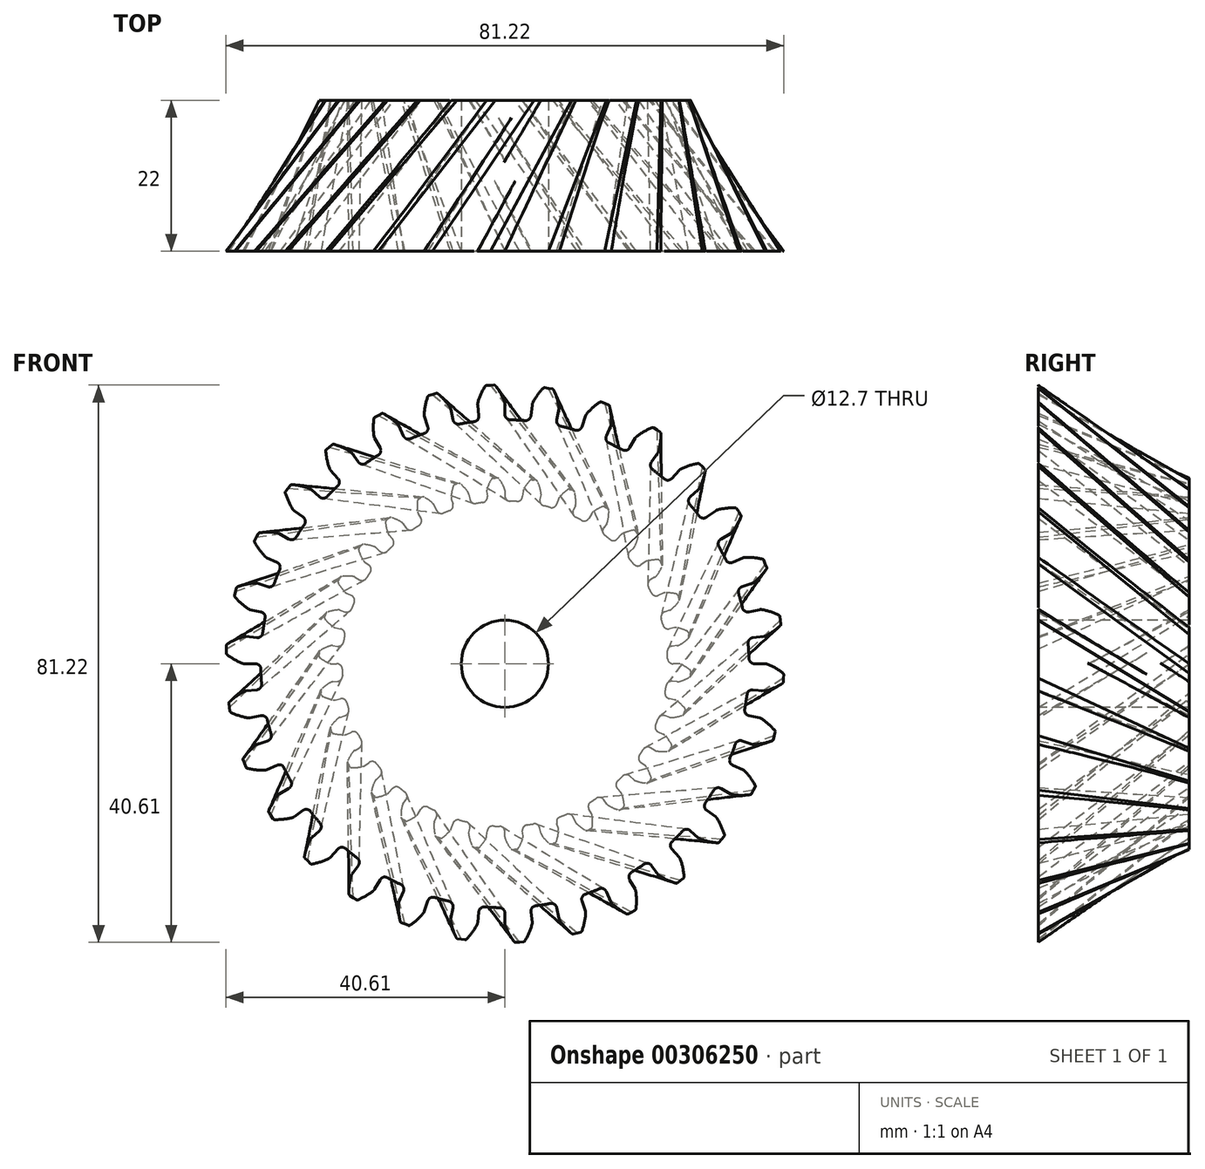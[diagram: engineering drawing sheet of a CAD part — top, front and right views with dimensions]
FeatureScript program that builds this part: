
annotation { "Feature Type Name" : "Feature", "Feature Type Description" : "" }
export const myFeature = defineFeature(function(context is Context, id is Id, definition is map)
    precondition{}
    {
        {
            var Q0;
            Q0=qCreatedBy(makeId("Front.planeOp"),FACE);
            var sketch = newSketch(context, id + "F0", { "sketchPlane" : qUnion([Q0])});
            skArc(sketch, "E0", {"start": v(-3.24, 23.49) * mm, "mid": v(-4.09, 23.36) * mm, "end": v(-4.93, 23.2) * mm});
            skArc(sketch, "E1.trimOffspring", {"start": v(-0.06, 25.55) * mm, "mid": v(-0.42, 26.29) * mm, "end": v(-0.88, 26.97) * mm});
            skLineSegment(sketch, "E2", {"start": v(-1.08, 27.07) * mm, "end": v(-1.42, 27.07) * mm});
            skLineSegment(sketch, "E3", {"start": v(0, 25.25) * mm, "end": v(0, 24.5) * mm});
            skLineSegment(sketch, "E4.MirrorCS", {"start": v(-1.76, 27.04) * mm, "end": v(-1.42, 27.07) * mm});
            skArc(sketch, "E5.MirrorCS", {"start": v(-2.61, 25.42) * mm, "mid": v(-2.33, 26.19) * mm, "end": v(-1.95, 26.92) * mm});
            skLineSegment(sketch, "E6.MirrorCS", {"start": v(-2.64, 25.1) * mm, "end": v(-2.56, 24.36) * mm});
            skArc(sketch, "E7.filletArc", {"start": v(-3.24, 23.49) * mm, "mid": v(-2.72, 23.79) * mm, "end": v(-2.56, 24.36) * mm});
            skPoint(sketch, "E8.visualSharp", {"position": v(0, 23.71) * mm});
            skPoint(sketch, "E9.visualSharp", {"position": v(-2.66, 25.26) * mm});
            skArc(sketch, "E9.filletArc", {"start": v(-2.65, 25.26) * mm, "mid": v(-2.65, 25.26) * mm, "end": v(-2.65, 25.26) * mm});
            skArc(sketch, "E10.filletArc", {"start": v(0, 24.5) * mm, "mid": v(0.22, 23.94) * mm, "end": v(0.77, 23.7) * mm});
            skArc(sketch, "E11.filletArc", {"start": v(-2.61, 25.42) * mm, "mid": v(-2.64, 25.26) * mm, "end": v(-2.64, 25.1) * mm});
            skPoint(sketch, "E12.visualSharp", {"position": v(0, 25.4) * mm});
            skArc(sketch, "E12.filletArc", {"start": v(0, 25.25) * mm, "mid": v(-0.02, 25.4) * mm, "end": v(-0.06, 25.55) * mm});
            skPoint(sketch, "E13.visualSharp", {"position": v(-1.88, 27.02) * mm});
            skArc(sketch, "E13.filletArc", {"start": v(-1.76, 27.04) * mm, "mid": v(-1.86, 27) * mm, "end": v(-1.95, 26.92) * mm});
            skPoint(sketch, "E14.visualSharp", {"position": v(-0.96, 27.07) * mm});
            skArc(sketch, "E14.filletArc", {"start": v(-0.88, 26.97) * mm, "mid": v(-0.97, 27.05) * mm, "end": v(-1.08, 27.07) * mm});
            skArc(sketch, "E15.1.0", {"start": v(-5.37, 24.98) * mm, "mid": v(-5.88, 25.63) * mm, "end": v(-6.47, 26.2) * mm});
            skPoint(sketch, "E15.1.1", {"position": v(-5.28, 24.84) * mm});
            skPoint(sketch, "E15.1.2", {"position": v(-7.85, 24.16) * mm});
            skLineSegment(sketch, "E15.1.3", {"start": v(-5.25, 24.7) * mm, "end": v(-5.1, 23.96) * mm});
            skArc(sketch, "E15.1.4", {"start": v(-7.84, 24.32) * mm, "mid": v(-7.72, 25.13) * mm, "end": v(-7.5, 25.92) * mm});
            skArc(sketch, "E15.1.5", {"start": v(-8.05, 22.3) * mm, "mid": v(-7.61, 22.7) * mm, "end": v(-7.57, 23.3) * mm});
            skPoint(sketch, "E15.1.6", {"position": v(-4.93, 23.2) * mm});
            skArc(sketch, "E15.1.7", {"start": v(-5.1, 23.96) * mm, "mid": v(-4.76, 23.46) * mm, "end": v(-4.18, 23.34) * mm});
            skPoint(sketch, "E15.1.8", {"position": v(-6.56, 26.28) * mm});
            skPoint(sketch, "E15.1.9", {"position": v(-7.46, 26.04) * mm});
            skLineSegment(sketch, "E15.1.10", {"start": v(-7.8, 24.01) * mm, "end": v(-7.57, 23.3) * mm});
            skArc(sketch, "E15.1.11", {"start": v(-5.25, 24.7) * mm, "mid": v(-5.3, 24.84) * mm, "end": v(-5.37, 24.98) * mm});
            skLineSegment(sketch, "E15.1.12", {"start": v(-7.34, 26.08) * mm, "end": v(-7.02, 26.19) * mm});
            skLineSegment(sketch, "E15.1.13", {"start": v(-6.69, 26.26) * mm, "end": v(-7.02, 26.19) * mm});
            skArc(sketch, "E15.1.14", {"start": v(-7.34, 26.08) * mm, "mid": v(-7.44, 26.02) * mm, "end": v(-7.5, 25.92) * mm});
            skArc(sketch, "E15.1.15", {"start": v(-6.47, 26.2) * mm, "mid": v(-6.57, 26.25) * mm, "end": v(-6.69, 26.26) * mm});
            skArc(sketch, "E15.1.16", {"start": v(-7.84, 24.32) * mm, "mid": v(-7.84, 24.16) * mm, "end": v(-7.8, 24.01) * mm});
            skArc(sketch, "E15.1.17", {"start": v(-7.85, 24.16) * mm, "mid": v(-7.85, 24.16) * mm, "end": v(-7.85, 24.15) * mm});
            skArc(sketch, "E15.1.18", {"start": v(-7.85, 24.16) * mm, "mid": v(-7.85, 24.16) * mm, "end": v(-7.85, 24.15) * mm});
            skArc(sketch, "E15.2.0", {"start": v(-10.45, 23.32) * mm, "mid": v(-11.08, 23.84) * mm, "end": v(-11.77, 24.28) * mm});
            skPoint(sketch, "E15.2.1", {"position": v(-10.33, 23.2) * mm});
            skPoint(sketch, "E15.2.2", {"position": v(-12.7, 22) * mm});
            skLineSegment(sketch, "E15.2.3", {"start": v(-10.27, 23.06) * mm, "end": v(-9.96, 22.37) * mm});
            skArc(sketch, "E15.2.4", {"start": v(-12.72, 22.16) * mm, "mid": v(-12.78, 22.98) * mm, "end": v(-12.73, 23.8) * mm});
            skArc(sketch, "E15.2.5", {"start": v(-12.51, 20.14) * mm, "mid": v(-12.16, 20.62) * mm, "end": v(-12.25, 21.21) * mm});
            skPoint(sketch, "E15.2.6", {"position": v(-9.64, 21.66) * mm});
            skArc(sketch, "E15.2.7", {"start": v(-9.96, 22.37) * mm, "mid": v(-9.53, 21.96) * mm, "end": v(-8.94, 21.96) * mm});
            skPoint(sketch, "E15.2.8", {"position": v(-11.88, 24.34) * mm});
            skPoint(sketch, "E15.2.9", {"position": v(-12.7, 23.92) * mm});
            skLineSegment(sketch, "E15.2.10", {"start": v(-12.62, 21.87) * mm, "end": v(-12.25, 21.21) * mm});
            skArc(sketch, "E15.2.11", {"start": v(-10.27, 23.06) * mm, "mid": v(-10.35, 23.2) * mm, "end": v(-10.45, 23.32) * mm});
            skLineSegment(sketch, "E15.2.12", {"start": v(-12.6, 23.99) * mm, "end": v(-12.3, 24.15) * mm});
            skLineSegment(sketch, "E15.2.13", {"start": v(-12, 24.3) * mm, "end": v(-12.3, 24.15) * mm});
            skArc(sketch, "E15.2.14", {"start": v(-12.6, 23.99) * mm, "mid": v(-12.68, 23.9) * mm, "end": v(-12.73, 23.8) * mm});
            skArc(sketch, "E15.2.15", {"start": v(-11.77, 24.28) * mm, "mid": v(-11.88, 24.31) * mm, "end": v(-12, 24.3) * mm});
            skArc(sketch, "E15.2.16", {"start": v(-12.72, 22.16) * mm, "mid": v(-12.69, 22) * mm, "end": v(-12.62, 21.87) * mm});
            skArc(sketch, "E15.2.17", {"start": v(-12.7, 22) * mm, "mid": v(-12.7, 22) * mm, "end": v(-12.7, 22) * mm});
            skArc(sketch, "E15.2.18", {"start": v(-12.7, 22) * mm, "mid": v(-12.7, 22) * mm, "end": v(-12.7, 22) * mm});
            skArc(sketch, "E16.1.3.0", {"start": v(-15.07, 20.64) * mm, "mid": v(-15.8, 21.02) * mm, "end": v(-16.56, 21.3) * mm});
            skPoint(sketch, "E16.4.3.0", {"position": v(-14.93, 20.55) * mm});
            skPoint(sketch, "E16.5.3.0", {"position": v(-17, 18.88) * mm});
            skLineSegment(sketch, "E16.6.3.0", {"start": v(-14.84, 20.43) * mm, "end": v(-14.4, 19.81) * mm});
            skArc(sketch, "E16.9.3.0", {"start": v(-17.05, 19.03) * mm, "mid": v(-17.28, 19.82) * mm, "end": v(-17.4, 20.63) * mm});
            skArc(sketch, "E16.13.3.0", {"start": v(-16.43, 17.1) * mm, "mid": v(-16.18, 17.64) * mm, "end": v(-16.39, 18.2) * mm});
            skPoint(sketch, "E16.17.3.0", {"position": v(-13.94, 19.18) * mm});
            skArc(sketch, "E16.18.3.0", {"start": v(-14.4, 19.81) * mm, "mid": v(-13.9, 19.5) * mm, "end": v(-13.3, 19.62) * mm});
            skPoint(sketch, "E16.22.3.0", {"position": v(-16.69, 21.34) * mm});
            skPoint(sketch, "E16.23.3.0", {"position": v(-17.4, 20.76) * mm});
            skLineSegment(sketch, "E16.24.3.0", {"start": v(-16.9, 18.76) * mm, "end": v(-16.39, 18.2) * mm});
            skArc(sketch, "E16.27.3.0", {"start": v(-14.84, 20.43) * mm, "mid": v(-14.94, 20.54) * mm, "end": v(-15.07, 20.64) * mm});
            skLineSegment(sketch, "E16.31.3.0", {"start": v(-17.31, 20.84) * mm, "end": v(-17.06, 21.07) * mm});
            skLineSegment(sketch, "E16.34.3.0", {"start": v(-16.79, 21.27) * mm, "end": v(-17.06, 21.07) * mm});
            skArc(sketch, "E16.37.3.0", {"start": v(-17.31, 20.84) * mm, "mid": v(-17.38, 20.75) * mm, "end": v(-17.4, 20.63) * mm});
            skArc(sketch, "E16.41.3.0", {"start": v(-16.56, 21.3) * mm, "mid": v(-16.68, 21.31) * mm, "end": v(-16.79, 21.27) * mm});
            skArc(sketch, "E16.45.3.0", {"start": v(-17.05, 19.03) * mm, "mid": v(-16.99, 18.89) * mm, "end": v(-16.9, 18.76) * mm});
            skArc(sketch, "E16.49.3.0", {"start": v(-17, 18.88) * mm, "mid": v(-17, 18.88) * mm, "end": v(-17, 18.87) * mm});
            skArc(sketch, "E16.53.3.0", {"start": v(-17, 18.88) * mm, "mid": v(-17, 18.88) * mm, "end": v(-17, 18.87) * mm});
            skArc(sketch, "E16.1.4.0", {"start": v(-19.03, 17.05) * mm, "mid": v(-19.82, 17.28) * mm, "end": v(-20.63, 17.4) * mm});
            skPoint(sketch, "E16.4.4.0", {"position": v(-18.88, 17) * mm});
            skPoint(sketch, "E16.5.4.0", {"position": v(-20.55, 14.93) * mm});
            skLineSegment(sketch, "E16.6.4.0", {"start": v(-18.76, 16.9) * mm, "end": v(-18.2, 16.39) * mm});
            skArc(sketch, "E16.9.4.0", {"start": v(-20.64, 15.07) * mm, "mid": v(-21.02, 15.8) * mm, "end": v(-21.3, 16.56) * mm});
            skArc(sketch, "E16.13.4.0", {"start": v(-19.62, 13.3) * mm, "mid": v(-19.5, 13.9) * mm, "end": v(-19.81, 14.4) * mm});
            skPoint(sketch, "E16.17.4.0", {"position": v(-17.62, 15.87) * mm});
            skArc(sketch, "E16.18.4.0", {"start": v(-18.2, 16.39) * mm, "mid": v(-17.64, 16.18) * mm, "end": v(-17.1, 16.43) * mm});
            skPoint(sketch, "E16.22.4.0", {"position": v(-20.76, 17.4) * mm});
            skPoint(sketch, "E16.23.4.0", {"position": v(-21.34, 16.69) * mm});
            skLineSegment(sketch, "E16.24.4.0", {"start": v(-20.43, 14.84) * mm, "end": v(-19.81, 14.4) * mm});
            skArc(sketch, "E16.27.4.0", {"start": v(-18.76, 16.9) * mm, "mid": v(-18.89, 16.99) * mm, "end": v(-19.03, 17.05) * mm});
            skLineSegment(sketch, "E16.31.4.0", {"start": v(-21.27, 16.79) * mm, "end": v(-21.07, 17.06) * mm});
            skLineSegment(sketch, "E16.34.4.0", {"start": v(-20.84, 17.31) * mm, "end": v(-21.07, 17.06) * mm});
            skArc(sketch, "E16.37.4.0", {"start": v(-21.27, 16.79) * mm, "mid": v(-21.31, 16.68) * mm, "end": v(-21.3, 16.56) * mm});
            skArc(sketch, "E16.41.4.0", {"start": v(-20.63, 17.4) * mm, "mid": v(-20.75, 17.38) * mm, "end": v(-20.84, 17.31) * mm});
            skArc(sketch, "E16.45.4.0", {"start": v(-20.64, 15.07) * mm, "mid": v(-20.54, 14.94) * mm, "end": v(-20.43, 14.84) * mm});
            skArc(sketch, "E16.49.4.0", {"start": v(-20.55, 14.93) * mm, "mid": v(-20.55, 14.93) * mm, "end": v(-20.55, 14.93) * mm});
            skArc(sketch, "E16.53.4.0", {"start": v(-20.55, 14.93) * mm, "mid": v(-20.55, 14.93) * mm, "end": v(-20.55, 14.93) * mm});
            skArc(sketch, "E16.1.5.0", {"start": v(-22.16, 12.72) * mm, "mid": v(-22.98, 12.78) * mm, "end": v(-23.8, 12.73) * mm});
            skPoint(sketch, "E16.4.5.0", {"position": v(-22, 12.7) * mm});
            skPoint(sketch, "E16.5.5.0", {"position": v(-23.2, 10.33) * mm});
            skLineSegment(sketch, "E16.6.5.0", {"start": v(-21.87, 12.62) * mm, "end": v(-21.21, 12.25) * mm});
            skArc(sketch, "E16.9.5.0", {"start": v(-23.32, 10.45) * mm, "mid": v(-23.84, 11.08) * mm, "end": v(-24.28, 11.77) * mm});
            skArc(sketch, "E16.13.5.0", {"start": v(-21.96, 8.94) * mm, "mid": v(-21.96, 9.53) * mm, "end": v(-22.37, 9.96) * mm});
            skPoint(sketch, "E16.17.5.0", {"position": v(-20.53, 11.86) * mm});
            skArc(sketch, "E16.18.5.0", {"start": v(-21.21, 12.25) * mm, "mid": v(-20.62, 12.16) * mm, "end": v(-20.14, 12.51) * mm});
            skPoint(sketch, "E16.22.5.0", {"position": v(-23.92, 12.7) * mm});
            skPoint(sketch, "E16.23.5.0", {"position": v(-24.34, 11.88) * mm});
            skLineSegment(sketch, "E16.24.5.0", {"start": v(-23.06, 10.27) * mm, "end": v(-22.37, 9.96) * mm});
            skArc(sketch, "E16.27.5.0", {"start": v(-21.87, 12.62) * mm, "mid": v(-22, 12.69) * mm, "end": v(-22.16, 12.72) * mm});
            skLineSegment(sketch, "E16.31.5.0", {"start": v(-24.3, 12) * mm, "end": v(-24.15, 12.3) * mm});
            skLineSegment(sketch, "E16.34.5.0", {"start": v(-23.99, 12.6) * mm, "end": v(-24.15, 12.3) * mm});
            skArc(sketch, "E16.37.5.0", {"start": v(-24.3, 12) * mm, "mid": v(-24.31, 11.88) * mm, "end": v(-24.28, 11.77) * mm});
            skArc(sketch, "E16.41.5.0", {"start": v(-23.8, 12.73) * mm, "mid": v(-23.9, 12.68) * mm, "end": v(-23.99, 12.6) * mm});
            skArc(sketch, "E16.45.5.0", {"start": v(-23.32, 10.45) * mm, "mid": v(-23.2, 10.35) * mm, "end": v(-23.06, 10.27) * mm});
            skArc(sketch, "E16.49.5.0", {"start": v(-23.2, 10.33) * mm, "mid": v(-23.2, 10.33) * mm, "end": v(-23.2, 10.33) * mm});
            skArc(sketch, "E16.53.5.0", {"start": v(-23.2, 10.33) * mm, "mid": v(-23.2, 10.33) * mm, "end": v(-23.2, 10.33) * mm});
            skArc(sketch, "E16.1.6.0", {"start": v(-24.32, 7.84) * mm, "mid": v(-25.13, 7.72) * mm, "end": v(-25.92, 7.5) * mm});
            skPoint(sketch, "E16.4.6.0", {"position": v(-24.16, 7.85) * mm});
            skPoint(sketch, "E16.5.6.0", {"position": v(-24.84, 5.28) * mm});
            skLineSegment(sketch, "E16.6.6.0", {"start": v(-24.01, 7.8) * mm, "end": v(-23.3, 7.57) * mm});
            skArc(sketch, "E16.9.6.0", {"start": v(-24.98, 5.37) * mm, "mid": v(-25.63, 5.88) * mm, "end": v(-26.2, 6.47) * mm});
            skArc(sketch, "E16.13.6.0", {"start": v(-23.34, 4.18) * mm, "mid": v(-23.46, 4.76) * mm, "end": v(-23.96, 5.1) * mm});
            skPoint(sketch, "E16.17.6.0", {"position": v(-22.55, 7.33) * mm});
            skArc(sketch, "E16.18.6.0", {"start": v(-23.3, 7.57) * mm, "mid": v(-22.7, 7.61) * mm, "end": v(-22.3, 8.05) * mm});
            skPoint(sketch, "E16.22.6.0", {"position": v(-26.04, 7.46) * mm});
            skPoint(sketch, "E16.23.6.0", {"position": v(-26.28, 6.56) * mm});
            skLineSegment(sketch, "E16.24.6.0", {"start": v(-24.7, 5.25) * mm, "end": v(-23.96, 5.1) * mm});
            skArc(sketch, "E16.27.6.0", {"start": v(-24.01, 7.8) * mm, "mid": v(-24.16, 7.84) * mm, "end": v(-24.32, 7.84) * mm});
            skLineSegment(sketch, "E16.31.6.0", {"start": v(-26.26, 6.69) * mm, "end": v(-26.19, 7.02) * mm});
            skLineSegment(sketch, "E16.34.6.0", {"start": v(-26.08, 7.34) * mm, "end": v(-26.19, 7.02) * mm});
            skArc(sketch, "E16.37.6.0", {"start": v(-26.26, 6.69) * mm, "mid": v(-26.25, 6.57) * mm, "end": v(-26.2, 6.47) * mm});
            skArc(sketch, "E16.41.6.0", {"start": v(-25.92, 7.5) * mm, "mid": v(-26.02, 7.44) * mm, "end": v(-26.08, 7.34) * mm});
            skArc(sketch, "E16.45.6.0", {"start": v(-24.98, 5.37) * mm, "mid": v(-24.84, 5.3) * mm, "end": v(-24.7, 5.25) * mm});
            skArc(sketch, "E16.49.6.0", {"start": v(-24.85, 5.28) * mm, "mid": v(-24.84, 5.28) * mm, "end": v(-24.84, 5.28) * mm});
            skArc(sketch, "E16.53.6.0", {"start": v(-24.85, 5.28) * mm, "mid": v(-24.84, 5.28) * mm, "end": v(-24.84, 5.28) * mm});
            skArc(sketch, "E16.1.7.0", {"start": v(-25.42, 2.61) * mm, "mid": v(-26.19, 2.33) * mm, "end": v(-26.92, 1.95) * mm});
            skPoint(sketch, "E16.4.7.0", {"position": v(-25.26, 2.66) * mm});
            skPoint(sketch, "E16.5.7.0", {"position": v(-25.4, 0) * mm});
            skLineSegment(sketch, "E16.6.7.0", {"start": v(-25.1, 2.64) * mm, "end": v(-24.36, 2.56) * mm});
            skArc(sketch, "E16.9.7.0", {"start": v(-25.55, 0.06) * mm, "mid": v(-26.29, 0.42) * mm, "end": v(-26.97, 0.88) * mm});
            skArc(sketch, "E16.13.7.0", {"start": v(-23.7, -0.77) * mm, "mid": v(-23.94, -0.22) * mm, "end": v(-24.5, 0) * mm});
            skPoint(sketch, "E16.17.7.0", {"position": v(-23.58, 2.48) * mm});
            skArc(sketch, "E16.18.7.0", {"start": v(-24.36, 2.56) * mm, "mid": v(-23.79, 2.72) * mm, "end": v(-23.49, 3.24) * mm});
            skPoint(sketch, "E16.22.7.0", {"position": v(-27.02, 1.88) * mm});
            skPoint(sketch, "E16.23.7.0", {"position": v(-27.07, 0.96) * mm});
            skLineSegment(sketch, "E16.24.7.0", {"start": v(-25.25, 0) * mm, "end": v(-24.5, 0) * mm});
            skArc(sketch, "E16.27.7.0", {"start": v(-25.1, 2.64) * mm, "mid": v(-25.26, 2.64) * mm, "end": v(-25.42, 2.61) * mm});
            skLineSegment(sketch, "E16.31.7.0", {"start": v(-27.07, 1.08) * mm, "end": v(-27.07, 1.42) * mm});
            skLineSegment(sketch, "E16.34.7.0", {"start": v(-27.04, 1.76) * mm, "end": v(-27.07, 1.42) * mm});
            skArc(sketch, "E16.37.7.0", {"start": v(-27.07, 1.08) * mm, "mid": v(-27.05, 0.97) * mm, "end": v(-26.97, 0.88) * mm});
            skArc(sketch, "E16.41.7.0", {"start": v(-26.92, 1.95) * mm, "mid": v(-27, 1.86) * mm, "end": v(-27.04, 1.76) * mm});
            skArc(sketch, "E16.45.7.0", {"start": v(-25.55, 0.06) * mm, "mid": v(-25.4, 0.02) * mm, "end": v(-25.25, 0) * mm});
            skArc(sketch, "E16.49.7.0", {"start": v(-25.4, 0) * mm, "mid": v(-25.4, 0) * mm, "end": v(-25.4, 0) * mm});
            skArc(sketch, "E16.53.7.0", {"start": v(-25.4, 0) * mm, "mid": v(-25.4, 0) * mm, "end": v(-25.4, 0) * mm});
            skArc(sketch, "E16.1.8.0", {"start": v(-25.4, -2.73) * mm, "mid": v(-26.1, -3.17) * mm, "end": v(-26.73, -3.7) * mm});
            skPoint(sketch, "E16.4.8.0", {"position": v(-25.26, -2.66) * mm});
            skPoint(sketch, "E16.5.8.0", {"position": v(-24.84, -5.28) * mm});
            skLineSegment(sketch, "E16.6.8.0", {"start": v(-25.1, -2.64) * mm, "end": v(-24.36, -2.56) * mm});
            skArc(sketch, "E16.9.8.0", {"start": v(-25, -5.25) * mm, "mid": v(-25.8, -5.05) * mm, "end": v(-26.57, -4.75) * mm});
            skArc(sketch, "E16.13.8.0", {"start": v(-23.02, -5.68) * mm, "mid": v(-23.37, -5.2) * mm, "end": v(-23.96, -5.1) * mm});
            skPoint(sketch, "E16.17.8.0", {"position": v(-23.58, -2.48) * mm});
            skArc(sketch, "E16.18.8.0", {"start": v(-24.36, -2.56) * mm, "mid": v(-23.83, -2.28) * mm, "end": v(-23.65, -1.71) * mm});
            skPoint(sketch, "E16.22.8.0", {"position": v(-26.82, -3.78) * mm});
            skPoint(sketch, "E16.23.8.0", {"position": v(-26.68, -4.7) * mm});
            skLineSegment(sketch, "E16.24.8.0", {"start": v(-24.7, -5.25) * mm, "end": v(-23.96, -5.1) * mm});
            skArc(sketch, "E16.27.8.0", {"start": v(-25.1, -2.64) * mm, "mid": v(-25.26, -2.67) * mm, "end": v(-25.4, -2.73) * mm});
            skLineSegment(sketch, "E16.31.8.0", {"start": v(-26.7, -4.57) * mm, "end": v(-26.78, -4.24) * mm});
            skLineSegment(sketch, "E16.34.8.0", {"start": v(-26.81, -3.9) * mm, "end": v(-26.78, -4.24) * mm});
            skArc(sketch, "E16.37.8.0", {"start": v(-26.7, -4.57) * mm, "mid": v(-26.66, -4.68) * mm, "end": v(-26.57, -4.75) * mm});
            skArc(sketch, "E16.41.8.0", {"start": v(-26.73, -3.7) * mm, "mid": v(-26.8, -3.79) * mm, "end": v(-26.81, -3.9) * mm});
            skArc(sketch, "E16.45.8.0", {"start": v(-25, -5.25) * mm, "mid": v(-24.85, -5.27) * mm, "end": v(-24.7, -5.25) * mm});
            skArc(sketch, "E16.49.8.0", {"start": v(-24.85, -5.28) * mm, "mid": v(-24.84, -5.28) * mm, "end": v(-24.84, -5.28) * mm});
            skArc(sketch, "E16.53.8.0", {"start": v(-24.85, -5.28) * mm, "mid": v(-24.84, -5.28) * mm, "end": v(-24.84, -5.28) * mm});
            skArc(sketch, "E16.1.9.0", {"start": v(-24.28, -7.95) * mm, "mid": v(-24.87, -8.53) * mm, "end": v(-25.38, -9.17) * mm});
            skPoint(sketch, "E16.4.9.0", {"position": v(-24.16, -7.85) * mm});
            skPoint(sketch, "E16.5.9.0", {"position": v(-23.2, -10.33) * mm});
            skLineSegment(sketch, "E16.6.9.0", {"start": v(-24.01, -7.8) * mm, "end": v(-23.3, -7.57) * mm});
            skArc(sketch, "E16.9.9.0", {"start": v(-23.37, -10.34) * mm, "mid": v(-24.19, -10.3) * mm, "end": v(-25, -10.17) * mm});
            skArc(sketch, "E16.13.9.0", {"start": v(-21.34, -10.34) * mm, "mid": v(-21.78, -9.94) * mm, "end": v(-22.37, -9.96) * mm});
            skPoint(sketch, "E16.17.9.0", {"position": v(-22.55, -7.33) * mm});
            skArc(sketch, "E16.18.9.0", {"start": v(-23.3, -7.57) * mm, "mid": v(-22.84, -7.19) * mm, "end": v(-22.78, -6.6) * mm});
            skPoint(sketch, "E16.22.9.0", {"position": v(-25.45, -9.28) * mm});
            skPoint(sketch, "E16.23.9.0", {"position": v(-25.12, -10.14) * mm});
            skLineSegment(sketch, "E16.24.9.0", {"start": v(-23.06, -10.27) * mm, "end": v(-22.37, -9.96) * mm});
            skArc(sketch, "E16.27.9.0", {"start": v(-24.01, -7.8) * mm, "mid": v(-24.15, -7.86) * mm, "end": v(-24.28, -7.95) * mm});
            skLineSegment(sketch, "E16.31.9.0", {"start": v(-25.17, -10.02) * mm, "end": v(-25.3, -9.72) * mm});
            skLineSegment(sketch, "E16.34.9.0", {"start": v(-25.41, -9.4) * mm, "end": v(-25.3, -9.72) * mm});
            skArc(sketch, "E16.37.9.0", {"start": v(-25.17, -10.02) * mm, "mid": v(-25.1, -10.12) * mm, "end": v(-25, -10.17) * mm});
            skArc(sketch, "E16.41.9.0", {"start": v(-25.38, -9.17) * mm, "mid": v(-25.42, -9.28) * mm, "end": v(-25.41, -9.4) * mm});
            skArc(sketch, "E16.45.9.0", {"start": v(-23.37, -10.34) * mm, "mid": v(-23.21, -10.32) * mm, "end": v(-23.06, -10.27) * mm});
            skArc(sketch, "E16.49.9.0", {"start": v(-23.2, -10.33) * mm, "mid": v(-23.2, -10.33) * mm, "end": v(-23.2, -10.33) * mm});
            skArc(sketch, "E16.53.9.0", {"start": v(-23.2, -10.33) * mm, "mid": v(-23.2, -10.33) * mm, "end": v(-23.2, -10.33) * mm});
            skArc(sketch, "E16.1.10.0", {"start": v(-22.1, -12.83) * mm, "mid": v(-22.55, -13.51) * mm, "end": v(-22.92, -14.25) * mm});
            skPoint(sketch, "E16.4.10.0", {"position": v(-22, -12.7) * mm});
            skPoint(sketch, "E16.5.10.0", {"position": v(-20.55, -14.93) * mm});
            skLineSegment(sketch, "E16.6.10.0", {"start": v(-21.87, -12.62) * mm, "end": v(-21.21, -12.25) * mm});
            skArc(sketch, "E16.9.10.0", {"start": v(-20.7, -14.97) * mm, "mid": v(-21.52, -15.1) * mm, "end": v(-22.34, -15.14) * mm});
            skArc(sketch, "E16.13.10.0", {"start": v(-18.72, -14.55) * mm, "mid": v(-19.24, -14.25) * mm, "end": v(-19.81, -14.4) * mm});
            skPoint(sketch, "E16.17.10.0", {"position": v(-20.53, -11.86) * mm});
            skArc(sketch, "E16.18.10.0", {"start": v(-21.21, -12.25) * mm, "mid": v(-20.84, -11.78) * mm, "end": v(-20.9, -11.18) * mm});
            skPoint(sketch, "E16.22.10.0", {"position": v(-22.97, -14.36) * mm});
            skPoint(sketch, "E16.23.10.0", {"position": v(-22.46, -15.14) * mm});
            skLineSegment(sketch, "E16.24.10.0", {"start": v(-20.43, -14.84) * mm, "end": v(-19.81, -14.4) * mm});
            skArc(sketch, "E16.27.10.0", {"start": v(-21.87, -12.62) * mm, "mid": v(-22, -12.71) * mm, "end": v(-22.1, -12.83) * mm});
            skLineSegment(sketch, "E16.31.10.0", {"start": v(-22.54, -15.04) * mm, "end": v(-22.74, -14.76) * mm});
            skLineSegment(sketch, "E16.34.10.0", {"start": v(-22.9, -14.47) * mm, "end": v(-22.74, -14.76) * mm});
            skArc(sketch, "E16.37.10.0", {"start": v(-22.54, -15.04) * mm, "mid": v(-22.45, -15.11) * mm, "end": v(-22.34, -15.14) * mm});
            skArc(sketch, "E16.41.10.0", {"start": v(-22.92, -14.25) * mm, "mid": v(-22.94, -14.36) * mm, "end": v(-22.9, -14.47) * mm});
            skArc(sketch, "E16.45.10.0", {"start": v(-20.7, -14.97) * mm, "mid": v(-20.56, -14.92) * mm, "end": v(-20.43, -14.84) * mm});
            skArc(sketch, "E16.49.10.0", {"start": v(-20.55, -14.93) * mm, "mid": v(-20.55, -14.93) * mm, "end": v(-20.55, -14.93) * mm});
            skArc(sketch, "E16.53.10.0", {"start": v(-20.55, -14.93) * mm, "mid": v(-20.55, -14.93) * mm, "end": v(-20.55, -14.93) * mm});
            skArc(sketch, "E16.1.11.0", {"start": v(-18.95, -17.14) * mm, "mid": v(-19.25, -17.9) * mm, "end": v(-19.46, -18.7) * mm});
            skPoint(sketch, "E16.4.11.0", {"position": v(-18.88, -17) * mm});
            skPoint(sketch, "E16.5.11.0", {"position": v(-17, -18.88) * mm});
            skLineSegment(sketch, "E16.6.11.0", {"start": v(-18.76, -16.9) * mm, "end": v(-18.2, -16.39) * mm});
            skArc(sketch, "E16.9.11.0", {"start": v(-17.14, -18.95) * mm, "mid": v(-17.9, -19.25) * mm, "end": v(-18.7, -19.46) * mm});
            skArc(sketch, "E16.13.11.0", {"start": v(-15.29, -18.13) * mm, "mid": v(-15.85, -17.94) * mm, "end": v(-16.39, -18.2) * mm});
            skPoint(sketch, "E16.17.11.0", {"position": v(-17.62, -15.87) * mm});
            skArc(sketch, "E16.18.11.0", {"start": v(-18.2, -16.39) * mm, "mid": v(-17.94, -15.85) * mm, "end": v(-18.13, -15.29) * mm});
            skPoint(sketch, "E16.22.11.0", {"position": v(-19.48, -18.83) * mm});
            skPoint(sketch, "E16.23.11.0", {"position": v(-18.83, -19.48) * mm});
            skLineSegment(sketch, "E16.24.11.0", {"start": v(-16.9, -18.76) * mm, "end": v(-16.39, -18.2) * mm});
            skArc(sketch, "E16.27.11.0", {"start": v(-18.76, -16.9) * mm, "mid": v(-18.87, -17) * mm, "end": v(-18.95, -17.14) * mm});
            skLineSegment(sketch, "E16.31.11.0", {"start": v(-18.92, -19.4) * mm, "end": v(-19.17, -19.17) * mm});
            skLineSegment(sketch, "E16.34.11.0", {"start": v(-19.4, -18.92) * mm, "end": v(-19.17, -19.17) * mm});
            skArc(sketch, "E16.37.11.0", {"start": v(-18.92, -19.4) * mm, "mid": v(-18.82, -19.45) * mm, "end": v(-18.7, -19.46) * mm});
            skArc(sketch, "E16.41.11.0", {"start": v(-19.46, -18.7) * mm, "mid": v(-19.45, -18.82) * mm, "end": v(-19.4, -18.92) * mm});
            skArc(sketch, "E16.45.11.0", {"start": v(-17.14, -18.95) * mm, "mid": v(-17, -18.87) * mm, "end": v(-16.9, -18.76) * mm});
            skArc(sketch, "E16.49.11.0", {"start": v(-17, -18.88) * mm, "mid": v(-17, -18.88) * mm, "end": v(-17, -18.87) * mm});
            skArc(sketch, "E16.53.11.0", {"start": v(-17, -18.88) * mm, "mid": v(-17, -18.88) * mm, "end": v(-17, -18.87) * mm});
            skArc(sketch, "E16.1.12.0", {"start": v(-14.97, -20.7) * mm, "mid": v(-15.1, -21.52) * mm, "end": v(-15.14, -22.34) * mm});
            skPoint(sketch, "E16.4.12.0", {"position": v(-14.93, -20.55) * mm});
            skPoint(sketch, "E16.5.12.0", {"position": v(-12.7, -22) * mm});
            skLineSegment(sketch, "E16.6.12.0", {"start": v(-14.84, -20.43) * mm, "end": v(-14.4, -19.81) * mm});
            skArc(sketch, "E16.9.12.0", {"start": v(-12.83, -22.1) * mm, "mid": v(-13.51, -22.55) * mm, "end": v(-14.25, -22.92) * mm});
            skArc(sketch, "E16.13.12.0", {"start": v(-11.18, -20.9) * mm, "mid": v(-11.78, -20.84) * mm, "end": v(-12.25, -21.21) * mm});
            skPoint(sketch, "E16.17.12.0", {"position": v(-13.94, -19.18) * mm});
            skArc(sketch, "E16.18.12.0", {"start": v(-14.4, -19.81) * mm, "mid": v(-14.25, -19.24) * mm, "end": v(-14.55, -18.72) * mm});
            skPoint(sketch, "E16.22.12.0", {"position": v(-15.14, -22.46) * mm});
            skPoint(sketch, "E16.23.12.0", {"position": v(-14.36, -22.97) * mm});
            skLineSegment(sketch, "E16.24.12.0", {"start": v(-12.62, -21.87) * mm, "end": v(-12.25, -21.21) * mm});
            skArc(sketch, "E16.27.12.0", {"start": v(-14.84, -20.43) * mm, "mid": v(-14.92, -20.56) * mm, "end": v(-14.97, -20.7) * mm});
            skLineSegment(sketch, "E16.31.12.0", {"start": v(-14.47, -22.9) * mm, "end": v(-14.76, -22.74) * mm});
            skLineSegment(sketch, "E16.34.12.0", {"start": v(-15.04, -22.54) * mm, "end": v(-14.76, -22.74) * mm});
            skArc(sketch, "E16.37.12.0", {"start": v(-14.47, -22.9) * mm, "mid": v(-14.36, -22.94) * mm, "end": v(-14.25, -22.92) * mm});
            skArc(sketch, "E16.41.12.0", {"start": v(-15.14, -22.34) * mm, "mid": v(-15.11, -22.45) * mm, "end": v(-15.04, -22.54) * mm});
            skArc(sketch, "E16.45.12.0", {"start": v(-12.83, -22.1) * mm, "mid": v(-12.71, -22) * mm, "end": v(-12.62, -21.87) * mm});
            skArc(sketch, "E16.49.12.0", {"start": v(-12.7, -22) * mm, "mid": v(-12.7, -22) * mm, "end": v(-12.7, -22) * mm});
            skArc(sketch, "E16.53.12.0", {"start": v(-12.7, -22) * mm, "mid": v(-12.7, -22) * mm, "end": v(-12.7, -22) * mm});
            skArc(sketch, "E16.1.13.0", {"start": v(-10.34, -23.37) * mm, "mid": v(-10.3, -24.19) * mm, "end": v(-10.17, -25) * mm});
            skPoint(sketch, "E16.4.13.0", {"position": v(-10.33, -23.2) * mm});
            skPoint(sketch, "E16.5.13.0", {"position": v(-7.85, -24.16) * mm});
            skLineSegment(sketch, "E16.6.13.0", {"start": v(-10.27, -23.06) * mm, "end": v(-9.96, -22.37) * mm});
            skArc(sketch, "E16.9.13.0", {"start": v(-7.95, -24.28) * mm, "mid": v(-8.53, -24.87) * mm, "end": v(-9.17, -25.38) * mm});
            skArc(sketch, "E16.13.13.0", {"start": v(-6.6, -22.78) * mm, "mid": v(-7.19, -22.84) * mm, "end": v(-7.57, -23.3) * mm});
            skPoint(sketch, "E16.17.13.0", {"position": v(-9.64, -21.66) * mm});
            skArc(sketch, "E16.18.13.0", {"start": v(-9.96, -22.37) * mm, "mid": v(-9.94, -21.78) * mm, "end": v(-10.34, -21.34) * mm});
            skPoint(sketch, "E16.22.13.0", {"position": v(-10.14, -25.12) * mm});
            skPoint(sketch, "E16.23.13.0", {"position": v(-9.28, -25.45) * mm});
            skLineSegment(sketch, "E16.24.13.0", {"start": v(-7.8, -24.01) * mm, "end": v(-7.57, -23.3) * mm});
            skArc(sketch, "E16.27.13.0", {"start": v(-10.27, -23.06) * mm, "mid": v(-10.32, -23.21) * mm, "end": v(-10.34, -23.37) * mm});
            skLineSegment(sketch, "E16.31.13.0", {"start": v(-9.4, -25.41) * mm, "end": v(-9.72, -25.3) * mm});
            skLineSegment(sketch, "E16.34.13.0", {"start": v(-10.02, -25.17) * mm, "end": v(-9.72, -25.3) * mm});
            skArc(sketch, "E16.37.13.0", {"start": v(-9.4, -25.41) * mm, "mid": v(-9.28, -25.42) * mm, "end": v(-9.17, -25.38) * mm});
            skArc(sketch, "E16.41.13.0", {"start": v(-10.17, -25) * mm, "mid": v(-10.12, -25.1) * mm, "end": v(-10.02, -25.17) * mm});
            skArc(sketch, "E16.45.13.0", {"start": v(-7.95, -24.28) * mm, "mid": v(-7.86, -24.15) * mm, "end": v(-7.8, -24.01) * mm});
            skArc(sketch, "E16.49.13.0", {"start": v(-7.85, -24.16) * mm, "mid": v(-7.85, -24.16) * mm, "end": v(-7.85, -24.15) * mm});
            skArc(sketch, "E16.53.13.0", {"start": v(-7.85, -24.16) * mm, "mid": v(-7.85, -24.16) * mm, "end": v(-7.85, -24.15) * mm});
            skArc(sketch, "E16.1.14.0", {"start": v(-5.25, -25) * mm, "mid": v(-5.05, -25.8) * mm, "end": v(-4.75, -26.57) * mm});
            skPoint(sketch, "E16.4.14.0", {"position": v(-5.28, -24.84) * mm});
            skPoint(sketch, "E16.5.14.0", {"position": v(-2.66, -25.26) * mm});
            skLineSegment(sketch, "E16.6.14.0", {"start": v(-5.25, -24.7) * mm, "end": v(-5.1, -23.96) * mm});
            skArc(sketch, "E16.9.14.0", {"start": v(-2.73, -25.4) * mm, "mid": v(-3.17, -26.1) * mm, "end": v(-3.7, -26.73) * mm});
            skArc(sketch, "E16.13.14.0", {"start": v(-1.71, -23.65) * mm, "mid": v(-2.28, -23.83) * mm, "end": v(-2.56, -24.36) * mm});
            skPoint(sketch, "E16.17.14.0", {"position": v(-4.93, -23.2) * mm});
            skArc(sketch, "E16.18.14.0", {"start": v(-5.1, -23.96) * mm, "mid": v(-5.2, -23.37) * mm, "end": v(-5.68, -23.02) * mm});
            skPoint(sketch, "E16.22.14.0", {"position": v(-4.7, -26.68) * mm});
            skPoint(sketch, "E16.23.14.0", {"position": v(-3.78, -26.82) * mm});
            skLineSegment(sketch, "E16.24.14.0", {"start": v(-2.64, -25.1) * mm, "end": v(-2.56, -24.36) * mm});
            skArc(sketch, "E16.27.14.0", {"start": v(-5.25, -24.7) * mm, "mid": v(-5.27, -24.85) * mm, "end": v(-5.25, -25) * mm});
            skLineSegment(sketch, "E16.31.14.0", {"start": v(-3.9, -26.81) * mm, "end": v(-4.24, -26.78) * mm});
            skLineSegment(sketch, "E16.34.14.0", {"start": v(-4.57, -26.7) * mm, "end": v(-4.24, -26.78) * mm});
            skArc(sketch, "E16.37.14.0", {"start": v(-3.9, -26.81) * mm, "mid": v(-3.79, -26.8) * mm, "end": v(-3.7, -26.73) * mm});
            skArc(sketch, "E16.41.14.0", {"start": v(-4.75, -26.57) * mm, "mid": v(-4.68, -26.66) * mm, "end": v(-4.57, -26.7) * mm});
            skArc(sketch, "E16.45.14.0", {"start": v(-2.73, -25.4) * mm, "mid": v(-2.67, -25.26) * mm, "end": v(-2.64, -25.1) * mm});
            skArc(sketch, "E16.49.14.0", {"start": v(-2.66, -25.26) * mm, "mid": v(-2.66, -25.26) * mm, "end": v(-2.65, -25.26) * mm});
            skArc(sketch, "E16.53.14.0", {"start": v(-2.66, -25.26) * mm, "mid": v(-2.66, -25.26) * mm, "end": v(-2.65, -25.26) * mm});
            skArc(sketch, "E16.1.15.0", {"start": v(0.06, -25.55) * mm, "mid": v(0.42, -26.29) * mm, "end": v(0.88, -26.97) * mm});
            skPoint(sketch, "E16.4.15.0", {"position": v(0, -25.4) * mm});
            skPoint(sketch, "E16.5.15.0", {"position": v(2.66, -25.26) * mm});
            skLineSegment(sketch, "E16.6.15.0", {"start": v(0, -25.25) * mm, "end": v(0, -24.5) * mm});
            skArc(sketch, "E16.9.15.0", {"start": v(2.61, -25.42) * mm, "mid": v(2.33, -26.19) * mm, "end": v(1.95, -26.92) * mm});
            skArc(sketch, "E16.13.15.0", {"start": v(3.24, -23.49) * mm, "mid": v(2.72, -23.79) * mm, "end": v(2.56, -24.36) * mm});
            skPoint(sketch, "E16.17.15.0", {"position": v(0, -23.71) * mm});
            skArc(sketch, "E16.18.15.0", {"start": v(0, -24.5) * mm, "mid": v(-0.22, -23.94) * mm, "end": v(-0.77, -23.7) * mm});
            skPoint(sketch, "E16.22.15.0", {"position": v(0.96, -27.07) * mm});
            skPoint(sketch, "E16.23.15.0", {"position": v(1.88, -27.02) * mm});
            skLineSegment(sketch, "E16.24.15.0", {"start": v(2.64, -25.1) * mm, "end": v(2.56, -24.36) * mm});
            skArc(sketch, "E16.27.15.0", {"start": v(0, -25.25) * mm, "mid": v(0.02, -25.4) * mm, "end": v(0.06, -25.55) * mm});
            skLineSegment(sketch, "E16.31.15.0", {"start": v(1.76, -27.04) * mm, "end": v(1.42, -27.07) * mm});
            skLineSegment(sketch, "E16.34.15.0", {"start": v(1.08, -27.07) * mm, "end": v(1.42, -27.07) * mm});
            skArc(sketch, "E16.37.15.0", {"start": v(1.76, -27.04) * mm, "mid": v(1.86, -27) * mm, "end": v(1.95, -26.92) * mm});
            skArc(sketch, "E16.41.15.0", {"start": v(0.88, -26.97) * mm, "mid": v(0.97, -27.05) * mm, "end": v(1.08, -27.07) * mm});
            skArc(sketch, "E16.45.15.0", {"start": v(2.61, -25.42) * mm, "mid": v(2.64, -25.26) * mm, "end": v(2.64, -25.1) * mm});
            skArc(sketch, "E16.49.15.0", {"start": v(2.65, -25.26) * mm, "mid": v(2.65, -25.26) * mm, "end": v(2.65, -25.26) * mm});
            skArc(sketch, "E16.53.15.0", {"start": v(2.65, -25.26) * mm, "mid": v(2.65, -25.26) * mm, "end": v(2.65, -25.26) * mm});
            skArc(sketch, "E16.1.16.0", {"start": v(5.37, -24.98) * mm, "mid": v(5.88, -25.63) * mm, "end": v(6.47, -26.2) * mm});
            skPoint(sketch, "E16.4.16.0", {"position": v(5.28, -24.84) * mm});
            skPoint(sketch, "E16.5.16.0", {"position": v(7.85, -24.16) * mm});
            skLineSegment(sketch, "E16.6.16.0", {"start": v(5.25, -24.7) * mm, "end": v(5.1, -23.96) * mm});
            skArc(sketch, "E16.9.16.0", {"start": v(7.84, -24.32) * mm, "mid": v(7.72, -25.13) * mm, "end": v(7.5, -25.92) * mm});
            skArc(sketch, "E16.13.16.0", {"start": v(8.05, -22.3) * mm, "mid": v(7.61, -22.7) * mm, "end": v(7.57, -23.3) * mm});
            skPoint(sketch, "E16.17.16.0", {"position": v(4.93, -23.2) * mm});
            skArc(sketch, "E16.18.16.0", {"start": v(5.1, -23.96) * mm, "mid": v(4.76, -23.46) * mm, "end": v(4.18, -23.34) * mm});
            skPoint(sketch, "E16.22.16.0", {"position": v(6.56, -26.28) * mm});
            skPoint(sketch, "E16.23.16.0", {"position": v(7.46, -26.04) * mm});
            skLineSegment(sketch, "E16.24.16.0", {"start": v(7.8, -24.01) * mm, "end": v(7.57, -23.3) * mm});
            skArc(sketch, "E16.27.16.0", {"start": v(5.25, -24.7) * mm, "mid": v(5.3, -24.84) * mm, "end": v(5.37, -24.98) * mm});
            skLineSegment(sketch, "E16.31.16.0", {"start": v(7.34, -26.08) * mm, "end": v(7.02, -26.19) * mm});
            skLineSegment(sketch, "E16.34.16.0", {"start": v(6.69, -26.26) * mm, "end": v(7.02, -26.19) * mm});
            skArc(sketch, "E16.37.16.0", {"start": v(7.34, -26.08) * mm, "mid": v(7.44, -26.02) * mm, "end": v(7.5, -25.92) * mm});
            skArc(sketch, "E16.41.16.0", {"start": v(6.47, -26.2) * mm, "mid": v(6.57, -26.25) * mm, "end": v(6.69, -26.26) * mm});
            skArc(sketch, "E16.45.16.0", {"start": v(7.84, -24.32) * mm, "mid": v(7.84, -24.16) * mm, "end": v(7.8, -24.01) * mm});
            skArc(sketch, "E16.49.16.0", {"start": v(7.85, -24.16) * mm, "mid": v(7.85, -24.16) * mm, "end": v(7.85, -24.15) * mm});
            skArc(sketch, "E16.53.16.0", {"start": v(7.85, -24.16) * mm, "mid": v(7.85, -24.16) * mm, "end": v(7.85, -24.15) * mm});
            skArc(sketch, "E16.1.17.0", {"start": v(10.45, -23.32) * mm, "mid": v(11.08, -23.84) * mm, "end": v(11.77, -24.28) * mm});
            skPoint(sketch, "E16.4.17.0", {"position": v(10.33, -23.2) * mm});
            skPoint(sketch, "E16.5.17.0", {"position": v(12.7, -22) * mm});
            skLineSegment(sketch, "E16.6.17.0", {"start": v(10.27, -23.06) * mm, "end": v(9.96, -22.37) * mm});
            skArc(sketch, "E16.9.17.0", {"start": v(12.72, -22.16) * mm, "mid": v(12.78, -22.98) * mm, "end": v(12.73, -23.8) * mm});
            skArc(sketch, "E16.13.17.0", {"start": v(12.51, -20.14) * mm, "mid": v(12.16, -20.62) * mm, "end": v(12.25, -21.21) * mm});
            skPoint(sketch, "E16.17.17.0", {"position": v(9.64, -21.66) * mm});
            skArc(sketch, "E16.18.17.0", {"start": v(9.96, -22.37) * mm, "mid": v(9.53, -21.96) * mm, "end": v(8.94, -21.96) * mm});
            skPoint(sketch, "E16.22.17.0", {"position": v(11.88, -24.34) * mm});
            skPoint(sketch, "E16.23.17.0", {"position": v(12.7, -23.92) * mm});
            skLineSegment(sketch, "E16.24.17.0", {"start": v(12.62, -21.87) * mm, "end": v(12.25, -21.21) * mm});
            skArc(sketch, "E16.27.17.0", {"start": v(10.27, -23.06) * mm, "mid": v(10.35, -23.2) * mm, "end": v(10.45, -23.32) * mm});
            skLineSegment(sketch, "E16.31.17.0", {"start": v(12.6, -23.99) * mm, "end": v(12.3, -24.15) * mm});
            skLineSegment(sketch, "E16.34.17.0", {"start": v(12, -24.3) * mm, "end": v(12.3, -24.15) * mm});
            skArc(sketch, "E16.37.17.0", {"start": v(12.6, -23.99) * mm, "mid": v(12.68, -23.9) * mm, "end": v(12.73, -23.8) * mm});
            skArc(sketch, "E16.41.17.0", {"start": v(11.77, -24.28) * mm, "mid": v(11.88, -24.31) * mm, "end": v(12, -24.3) * mm});
            skArc(sketch, "E16.45.17.0", {"start": v(12.72, -22.16) * mm, "mid": v(12.69, -22) * mm, "end": v(12.62, -21.87) * mm});
            skArc(sketch, "E16.49.17.0", {"start": v(12.7, -22) * mm, "mid": v(12.7, -22) * mm, "end": v(12.7, -22) * mm});
            skArc(sketch, "E16.53.17.0", {"start": v(12.7, -22) * mm, "mid": v(12.7, -22) * mm, "end": v(12.7, -22) * mm});
            skArc(sketch, "E16.1.18.0", {"start": v(15.07, -20.64) * mm, "mid": v(15.8, -21.02) * mm, "end": v(16.56, -21.3) * mm});
            skPoint(sketch, "E16.4.18.0", {"position": v(14.93, -20.55) * mm});
            skPoint(sketch, "E16.5.18.0", {"position": v(17, -18.88) * mm});
            skLineSegment(sketch, "E16.6.18.0", {"start": v(14.84, -20.43) * mm, "end": v(14.4, -19.81) * mm});
            skArc(sketch, "E16.9.18.0", {"start": v(17.05, -19.03) * mm, "mid": v(17.28, -19.82) * mm, "end": v(17.4, -20.63) * mm});
            skArc(sketch, "E16.13.18.0", {"start": v(16.43, -17.1) * mm, "mid": v(16.18, -17.64) * mm, "end": v(16.39, -18.2) * mm});
            skPoint(sketch, "E16.17.18.0", {"position": v(13.94, -19.18) * mm});
            skArc(sketch, "E16.18.18.0", {"start": v(14.4, -19.81) * mm, "mid": v(13.9, -19.5) * mm, "end": v(13.3, -19.62) * mm});
            skPoint(sketch, "E16.22.18.0", {"position": v(16.69, -21.34) * mm});
            skPoint(sketch, "E16.23.18.0", {"position": v(17.4, -20.76) * mm});
            skLineSegment(sketch, "E16.24.18.0", {"start": v(16.9, -18.76) * mm, "end": v(16.39, -18.2) * mm});
            skArc(sketch, "E16.27.18.0", {"start": v(14.84, -20.43) * mm, "mid": v(14.94, -20.54) * mm, "end": v(15.07, -20.64) * mm});
            skLineSegment(sketch, "E16.31.18.0", {"start": v(17.31, -20.84) * mm, "end": v(17.06, -21.07) * mm});
            skLineSegment(sketch, "E16.34.18.0", {"start": v(16.79, -21.27) * mm, "end": v(17.06, -21.07) * mm});
            skArc(sketch, "E16.37.18.0", {"start": v(17.31, -20.84) * mm, "mid": v(17.38, -20.75) * mm, "end": v(17.4, -20.63) * mm});
            skArc(sketch, "E16.41.18.0", {"start": v(16.56, -21.3) * mm, "mid": v(16.68, -21.31) * mm, "end": v(16.79, -21.27) * mm});
            skArc(sketch, "E16.45.18.0", {"start": v(17.05, -19.03) * mm, "mid": v(16.99, -18.89) * mm, "end": v(16.9, -18.76) * mm});
            skArc(sketch, "E16.49.18.0", {"start": v(17, -18.88) * mm, "mid": v(17, -18.88) * mm, "end": v(17, -18.87) * mm});
            skArc(sketch, "E16.53.18.0", {"start": v(17, -18.88) * mm, "mid": v(17, -18.88) * mm, "end": v(17, -18.87) * mm});
            skArc(sketch, "E16.1.19.0", {"start": v(19.03, -17.05) * mm, "mid": v(19.82, -17.28) * mm, "end": v(20.63, -17.4) * mm});
            skPoint(sketch, "E16.4.19.0", {"position": v(18.88, -17) * mm});
            skPoint(sketch, "E16.5.19.0", {"position": v(20.55, -14.93) * mm});
            skLineSegment(sketch, "E16.6.19.0", {"start": v(18.76, -16.9) * mm, "end": v(18.2, -16.39) * mm});
            skArc(sketch, "E16.9.19.0", {"start": v(20.64, -15.07) * mm, "mid": v(21.02, -15.8) * mm, "end": v(21.3, -16.56) * mm});
            skArc(sketch, "E16.13.19.0", {"start": v(19.62, -13.3) * mm, "mid": v(19.5, -13.9) * mm, "end": v(19.81, -14.4) * mm});
            skPoint(sketch, "E16.17.19.0", {"position": v(17.62, -15.87) * mm});
            skArc(sketch, "E16.18.19.0", {"start": v(18.2, -16.39) * mm, "mid": v(17.64, -16.18) * mm, "end": v(17.1, -16.43) * mm});
            skPoint(sketch, "E16.22.19.0", {"position": v(20.76, -17.4) * mm});
            skPoint(sketch, "E16.23.19.0", {"position": v(21.34, -16.69) * mm});
            skLineSegment(sketch, "E16.24.19.0", {"start": v(20.43, -14.84) * mm, "end": v(19.81, -14.4) * mm});
            skArc(sketch, "E16.27.19.0", {"start": v(18.76, -16.9) * mm, "mid": v(18.89, -16.99) * mm, "end": v(19.03, -17.05) * mm});
            skLineSegment(sketch, "E16.31.19.0", {"start": v(21.27, -16.79) * mm, "end": v(21.07, -17.06) * mm});
            skLineSegment(sketch, "E16.34.19.0", {"start": v(20.84, -17.31) * mm, "end": v(21.07, -17.06) * mm});
            skArc(sketch, "E16.37.19.0", {"start": v(21.27, -16.79) * mm, "mid": v(21.31, -16.68) * mm, "end": v(21.3, -16.56) * mm});
            skArc(sketch, "E16.41.19.0", {"start": v(20.63, -17.4) * mm, "mid": v(20.75, -17.38) * mm, "end": v(20.84, -17.31) * mm});
            skArc(sketch, "E16.45.19.0", {"start": v(20.64, -15.07) * mm, "mid": v(20.54, -14.94) * mm, "end": v(20.43, -14.84) * mm});
            skArc(sketch, "E16.49.19.0", {"start": v(20.55, -14.93) * mm, "mid": v(20.55, -14.93) * mm, "end": v(20.55, -14.93) * mm});
            skArc(sketch, "E16.53.19.0", {"start": v(20.55, -14.93) * mm, "mid": v(20.55, -14.93) * mm, "end": v(20.55, -14.93) * mm});
            skArc(sketch, "E16.1.20.0", {"start": v(22.16, -12.72) * mm, "mid": v(22.98, -12.78) * mm, "end": v(23.8, -12.73) * mm});
            skPoint(sketch, "E16.4.20.0", {"position": v(22, -12.7) * mm});
            skPoint(sketch, "E16.5.20.0", {"position": v(23.2, -10.33) * mm});
            skLineSegment(sketch, "E16.6.20.0", {"start": v(21.87, -12.62) * mm, "end": v(21.21, -12.25) * mm});
            skArc(sketch, "E16.9.20.0", {"start": v(23.32, -10.45) * mm, "mid": v(23.84, -11.08) * mm, "end": v(24.28, -11.77) * mm});
            skArc(sketch, "E16.13.20.0", {"start": v(21.96, -8.94) * mm, "mid": v(21.96, -9.53) * mm, "end": v(22.37, -9.96) * mm});
            skPoint(sketch, "E16.17.20.0", {"position": v(20.53, -11.86) * mm});
            skArc(sketch, "E16.18.20.0", {"start": v(21.21, -12.25) * mm, "mid": v(20.62, -12.16) * mm, "end": v(20.14, -12.51) * mm});
            skPoint(sketch, "E16.22.20.0", {"position": v(23.92, -12.7) * mm});
            skPoint(sketch, "E16.23.20.0", {"position": v(24.34, -11.88) * mm});
            skLineSegment(sketch, "E16.24.20.0", {"start": v(23.06, -10.27) * mm, "end": v(22.37, -9.96) * mm});
            skArc(sketch, "E16.27.20.0", {"start": v(21.87, -12.62) * mm, "mid": v(22, -12.69) * mm, "end": v(22.16, -12.72) * mm});
            skLineSegment(sketch, "E16.31.20.0", {"start": v(24.3, -12) * mm, "end": v(24.15, -12.3) * mm});
            skLineSegment(sketch, "E16.34.20.0", {"start": v(23.99, -12.6) * mm, "end": v(24.15, -12.3) * mm});
            skArc(sketch, "E16.37.20.0", {"start": v(24.3, -12) * mm, "mid": v(24.31, -11.88) * mm, "end": v(24.28, -11.77) * mm});
            skArc(sketch, "E16.41.20.0", {"start": v(23.8, -12.73) * mm, "mid": v(23.9, -12.68) * mm, "end": v(23.99, -12.6) * mm});
            skArc(sketch, "E16.45.20.0", {"start": v(23.32, -10.45) * mm, "mid": v(23.2, -10.35) * mm, "end": v(23.06, -10.27) * mm});
            skArc(sketch, "E16.49.20.0", {"start": v(23.2, -10.33) * mm, "mid": v(23.2, -10.33) * mm, "end": v(23.2, -10.33) * mm});
            skArc(sketch, "E16.53.20.0", {"start": v(23.2, -10.33) * mm, "mid": v(23.2, -10.33) * mm, "end": v(23.2, -10.33) * mm});
            skArc(sketch, "E16.1.21.0", {"start": v(24.32, -7.84) * mm, "mid": v(25.13, -7.72) * mm, "end": v(25.92, -7.5) * mm});
            skPoint(sketch, "E16.4.21.0", {"position": v(24.16, -7.85) * mm});
            skPoint(sketch, "E16.5.21.0", {"position": v(24.84, -5.28) * mm});
            skLineSegment(sketch, "E16.6.21.0", {"start": v(24.01, -7.8) * mm, "end": v(23.3, -7.57) * mm});
            skArc(sketch, "E16.9.21.0", {"start": v(24.98, -5.37) * mm, "mid": v(25.63, -5.88) * mm, "end": v(26.2, -6.47) * mm});
            skArc(sketch, "E16.13.21.0", {"start": v(23.34, -4.18) * mm, "mid": v(23.46, -4.76) * mm, "end": v(23.96, -5.1) * mm});
            skPoint(sketch, "E16.17.21.0", {"position": v(22.55, -7.33) * mm});
            skArc(sketch, "E16.18.21.0", {"start": v(23.3, -7.57) * mm, "mid": v(22.7, -7.61) * mm, "end": v(22.3, -8.05) * mm});
            skPoint(sketch, "E16.22.21.0", {"position": v(26.04, -7.46) * mm});
            skPoint(sketch, "E16.23.21.0", {"position": v(26.28, -6.56) * mm});
            skLineSegment(sketch, "E16.24.21.0", {"start": v(24.7, -5.25) * mm, "end": v(23.96, -5.1) * mm});
            skArc(sketch, "E16.27.21.0", {"start": v(24.01, -7.8) * mm, "mid": v(24.16, -7.84) * mm, "end": v(24.32, -7.84) * mm});
            skLineSegment(sketch, "E16.31.21.0", {"start": v(26.26, -6.69) * mm, "end": v(26.19, -7.02) * mm});
            skLineSegment(sketch, "E16.34.21.0", {"start": v(26.08, -7.34) * mm, "end": v(26.19, -7.02) * mm});
            skArc(sketch, "E16.37.21.0", {"start": v(26.26, -6.69) * mm, "mid": v(26.25, -6.57) * mm, "end": v(26.2, -6.47) * mm});
            skArc(sketch, "E16.41.21.0", {"start": v(25.92, -7.5) * mm, "mid": v(26.02, -7.44) * mm, "end": v(26.08, -7.34) * mm});
            skArc(sketch, "E16.45.21.0", {"start": v(24.98, -5.37) * mm, "mid": v(24.84, -5.3) * mm, "end": v(24.7, -5.25) * mm});
            skArc(sketch, "E16.49.21.0", {"start": v(24.85, -5.28) * mm, "mid": v(24.84, -5.28) * mm, "end": v(24.84, -5.28) * mm});
            skArc(sketch, "E16.53.21.0", {"start": v(24.85, -5.28) * mm, "mid": v(24.84, -5.28) * mm, "end": v(24.84, -5.28) * mm});
            skArc(sketch, "E16.1.22.0", {"start": v(25.42, -2.61) * mm, "mid": v(26.19, -2.33) * mm, "end": v(26.92, -1.95) * mm});
            skPoint(sketch, "E16.4.22.0", {"position": v(25.26, -2.66) * mm});
            skPoint(sketch, "E16.5.22.0", {"position": v(25.4, 0) * mm});
            skLineSegment(sketch, "E16.6.22.0", {"start": v(25.1, -2.64) * mm, "end": v(24.36, -2.56) * mm});
            skArc(sketch, "E16.9.22.0", {"start": v(25.55, -0.06) * mm, "mid": v(26.29, -0.42) * mm, "end": v(26.97, -0.88) * mm});
            skArc(sketch, "E16.13.22.0", {"start": v(23.7, 0.77) * mm, "mid": v(23.94, 0.22) * mm, "end": v(24.5, 0) * mm});
            skPoint(sketch, "E16.17.22.0", {"position": v(23.58, -2.48) * mm});
            skArc(sketch, "E16.18.22.0", {"start": v(24.36, -2.56) * mm, "mid": v(23.79, -2.72) * mm, "end": v(23.49, -3.24) * mm});
            skPoint(sketch, "E16.22.22.0", {"position": v(27.02, -1.88) * mm});
            skPoint(sketch, "E16.23.22.0", {"position": v(27.07, -0.96) * mm});
            skLineSegment(sketch, "E16.24.22.0", {"start": v(25.25, 0) * mm, "end": v(24.5, 0) * mm});
            skArc(sketch, "E16.27.22.0", {"start": v(25.1, -2.64) * mm, "mid": v(25.26, -2.64) * mm, "end": v(25.42, -2.61) * mm});
            skLineSegment(sketch, "E16.31.22.0", {"start": v(27.07, -1.08) * mm, "end": v(27.07, -1.42) * mm});
            skLineSegment(sketch, "E16.34.22.0", {"start": v(27.04, -1.76) * mm, "end": v(27.07, -1.42) * mm});
            skArc(sketch, "E16.37.22.0", {"start": v(27.07, -1.08) * mm, "mid": v(27.05, -0.97) * mm, "end": v(26.97, -0.88) * mm});
            skArc(sketch, "E16.41.22.0", {"start": v(26.92, -1.95) * mm, "mid": v(27, -1.86) * mm, "end": v(27.04, -1.76) * mm});
            skArc(sketch, "E16.45.22.0", {"start": v(25.55, -0.06) * mm, "mid": v(25.4, -0.02) * mm, "end": v(25.25, 0) * mm});
            skArc(sketch, "E16.49.22.0", {"start": v(25.4, 0) * mm, "mid": v(25.4, 0) * mm, "end": v(25.4, 0) * mm});
            skArc(sketch, "E16.53.22.0", {"start": v(25.4, 0) * mm, "mid": v(25.4, 0) * mm, "end": v(25.4, 0) * mm});
            skArc(sketch, "E16.1.23.0", {"start": v(25.4, 2.73) * mm, "mid": v(26.1, 3.17) * mm, "end": v(26.73, 3.7) * mm});
            skPoint(sketch, "E16.4.23.0", {"position": v(25.26, 2.66) * mm});
            skPoint(sketch, "E16.5.23.0", {"position": v(24.84, 5.28) * mm});
            skLineSegment(sketch, "E16.6.23.0", {"start": v(25.1, 2.64) * mm, "end": v(24.36, 2.56) * mm});
            skArc(sketch, "E16.9.23.0", {"start": v(25, 5.25) * mm, "mid": v(25.8, 5.05) * mm, "end": v(26.57, 4.75) * mm});
            skArc(sketch, "E16.13.23.0", {"start": v(23.02, 5.68) * mm, "mid": v(23.37, 5.2) * mm, "end": v(23.96, 5.1) * mm});
            skPoint(sketch, "E16.17.23.0", {"position": v(23.58, 2.48) * mm});
            skArc(sketch, "E16.18.23.0", {"start": v(24.36, 2.56) * mm, "mid": v(23.83, 2.28) * mm, "end": v(23.65, 1.71) * mm});
            skPoint(sketch, "E16.22.23.0", {"position": v(26.82, 3.78) * mm});
            skPoint(sketch, "E16.23.23.0", {"position": v(26.68, 4.7) * mm});
            skLineSegment(sketch, "E16.24.23.0", {"start": v(24.7, 5.25) * mm, "end": v(23.96, 5.1) * mm});
            skArc(sketch, "E16.27.23.0", {"start": v(25.1, 2.64) * mm, "mid": v(25.26, 2.67) * mm, "end": v(25.4, 2.73) * mm});
            skLineSegment(sketch, "E16.31.23.0", {"start": v(26.7, 4.57) * mm, "end": v(26.78, 4.24) * mm});
            skLineSegment(sketch, "E16.34.23.0", {"start": v(26.81, 3.9) * mm, "end": v(26.78, 4.24) * mm});
            skArc(sketch, "E16.37.23.0", {"start": v(26.7, 4.57) * mm, "mid": v(26.66, 4.68) * mm, "end": v(26.57, 4.75) * mm});
            skArc(sketch, "E16.41.23.0", {"start": v(26.73, 3.7) * mm, "mid": v(26.8, 3.79) * mm, "end": v(26.81, 3.9) * mm});
            skArc(sketch, "E16.45.23.0", {"start": v(25, 5.25) * mm, "mid": v(24.85, 5.27) * mm, "end": v(24.7, 5.25) * mm});
            skArc(sketch, "E16.49.23.0", {"start": v(24.85, 5.28) * mm, "mid": v(24.84, 5.28) * mm, "end": v(24.84, 5.28) * mm});
            skArc(sketch, "E16.53.23.0", {"start": v(24.85, 5.28) * mm, "mid": v(24.84, 5.28) * mm, "end": v(24.84, 5.28) * mm});
            skArc(sketch, "E16.1.24.0", {"start": v(24.28, 7.95) * mm, "mid": v(24.87, 8.53) * mm, "end": v(25.38, 9.17) * mm});
            skPoint(sketch, "E16.4.24.0", {"position": v(24.16, 7.85) * mm});
            skPoint(sketch, "E16.5.24.0", {"position": v(23.2, 10.33) * mm});
            skLineSegment(sketch, "E16.6.24.0", {"start": v(24.01, 7.8) * mm, "end": v(23.3, 7.57) * mm});
            skArc(sketch, "E16.9.24.0", {"start": v(23.37, 10.34) * mm, "mid": v(24.19, 10.3) * mm, "end": v(25, 10.17) * mm});
            skArc(sketch, "E16.13.24.0", {"start": v(21.34, 10.34) * mm, "mid": v(21.78, 9.94) * mm, "end": v(22.37, 9.96) * mm});
            skPoint(sketch, "E16.17.24.0", {"position": v(22.55, 7.33) * mm});
            skArc(sketch, "E16.18.24.0", {"start": v(23.3, 7.57) * mm, "mid": v(22.84, 7.19) * mm, "end": v(22.78, 6.6) * mm});
            skPoint(sketch, "E16.22.24.0", {"position": v(25.45, 9.28) * mm});
            skPoint(sketch, "E16.23.24.0", {"position": v(25.12, 10.14) * mm});
            skLineSegment(sketch, "E16.24.24.0", {"start": v(23.06, 10.27) * mm, "end": v(22.37, 9.96) * mm});
            skArc(sketch, "E16.27.24.0", {"start": v(24.01, 7.8) * mm, "mid": v(24.15, 7.86) * mm, "end": v(24.28, 7.95) * mm});
            skLineSegment(sketch, "E16.31.24.0", {"start": v(25.17, 10.02) * mm, "end": v(25.3, 9.72) * mm});
            skLineSegment(sketch, "E16.34.24.0", {"start": v(25.41, 9.4) * mm, "end": v(25.3, 9.72) * mm});
            skArc(sketch, "E16.37.24.0", {"start": v(25.17, 10.02) * mm, "mid": v(25.1, 10.12) * mm, "end": v(25, 10.17) * mm});
            skArc(sketch, "E16.41.24.0", {"start": v(25.38, 9.17) * mm, "mid": v(25.42, 9.28) * mm, "end": v(25.41, 9.4) * mm});
            skArc(sketch, "E16.45.24.0", {"start": v(23.37, 10.34) * mm, "mid": v(23.21, 10.32) * mm, "end": v(23.06, 10.27) * mm});
            skArc(sketch, "E16.49.24.0", {"start": v(23.2, 10.33) * mm, "mid": v(23.2, 10.33) * mm, "end": v(23.2, 10.33) * mm});
            skArc(sketch, "E16.53.24.0", {"start": v(23.2, 10.33) * mm, "mid": v(23.2, 10.33) * mm, "end": v(23.2, 10.33) * mm});
            skArc(sketch, "E16.1.25.0", {"start": v(22.1, 12.83) * mm, "mid": v(22.55, 13.51) * mm, "end": v(22.92, 14.25) * mm});
            skPoint(sketch, "E16.4.25.0", {"position": v(22, 12.7) * mm});
            skPoint(sketch, "E16.5.25.0", {"position": v(20.55, 14.93) * mm});
            skLineSegment(sketch, "E16.6.25.0", {"start": v(21.87, 12.62) * mm, "end": v(21.21, 12.25) * mm});
            skArc(sketch, "E16.9.25.0", {"start": v(20.7, 14.97) * mm, "mid": v(21.52, 15.1) * mm, "end": v(22.34, 15.14) * mm});
            skArc(sketch, "E16.13.25.0", {"start": v(18.72, 14.55) * mm, "mid": v(19.24, 14.25) * mm, "end": v(19.81, 14.4) * mm});
            skPoint(sketch, "E16.17.25.0", {"position": v(20.53, 11.86) * mm});
            skArc(sketch, "E16.18.25.0", {"start": v(21.21, 12.25) * mm, "mid": v(20.84, 11.78) * mm, "end": v(20.9, 11.18) * mm});
            skPoint(sketch, "E16.22.25.0", {"position": v(22.97, 14.36) * mm});
            skPoint(sketch, "E16.23.25.0", {"position": v(22.46, 15.14) * mm});
            skLineSegment(sketch, "E16.24.25.0", {"start": v(20.43, 14.84) * mm, "end": v(19.81, 14.4) * mm});
            skArc(sketch, "E16.27.25.0", {"start": v(21.87, 12.62) * mm, "mid": v(22, 12.71) * mm, "end": v(22.1, 12.83) * mm});
            skLineSegment(sketch, "E16.31.25.0", {"start": v(22.54, 15.04) * mm, "end": v(22.74, 14.76) * mm});
            skLineSegment(sketch, "E16.34.25.0", {"start": v(22.9, 14.47) * mm, "end": v(22.74, 14.76) * mm});
            skArc(sketch, "E16.37.25.0", {"start": v(22.54, 15.04) * mm, "mid": v(22.45, 15.11) * mm, "end": v(22.34, 15.14) * mm});
            skArc(sketch, "E16.41.25.0", {"start": v(22.92, 14.25) * mm, "mid": v(22.94, 14.36) * mm, "end": v(22.9, 14.47) * mm});
            skArc(sketch, "E16.45.25.0", {"start": v(20.7, 14.97) * mm, "mid": v(20.56, 14.92) * mm, "end": v(20.43, 14.84) * mm});
            skArc(sketch, "E16.49.25.0", {"start": v(20.55, 14.93) * mm, "mid": v(20.55, 14.93) * mm, "end": v(20.55, 14.93) * mm});
            skArc(sketch, "E16.53.25.0", {"start": v(20.55, 14.93) * mm, "mid": v(20.55, 14.93) * mm, "end": v(20.55, 14.93) * mm});
            skArc(sketch, "E16.1.26.0", {"start": v(18.95, 17.14) * mm, "mid": v(19.25, 17.9) * mm, "end": v(19.46, 18.7) * mm});
            skPoint(sketch, "E16.4.26.0", {"position": v(18.88, 17) * mm});
            skPoint(sketch, "E16.5.26.0", {"position": v(17, 18.88) * mm});
            skLineSegment(sketch, "E16.6.26.0", {"start": v(18.76, 16.9) * mm, "end": v(18.2, 16.39) * mm});
            skArc(sketch, "E16.9.26.0", {"start": v(17.14, 18.95) * mm, "mid": v(17.9, 19.25) * mm, "end": v(18.7, 19.46) * mm});
            skArc(sketch, "E16.13.26.0", {"start": v(15.29, 18.13) * mm, "mid": v(15.85, 17.94) * mm, "end": v(16.39, 18.2) * mm});
            skPoint(sketch, "E16.17.26.0", {"position": v(17.62, 15.87) * mm});
            skArc(sketch, "E16.18.26.0", {"start": v(18.2, 16.39) * mm, "mid": v(17.94, 15.85) * mm, "end": v(18.13, 15.29) * mm});
            skPoint(sketch, "E16.22.26.0", {"position": v(19.48, 18.83) * mm});
            skPoint(sketch, "E16.23.26.0", {"position": v(18.83, 19.48) * mm});
            skLineSegment(sketch, "E16.24.26.0", {"start": v(16.9, 18.76) * mm, "end": v(16.39, 18.2) * mm});
            skArc(sketch, "E16.27.26.0", {"start": v(18.76, 16.9) * mm, "mid": v(18.87, 17) * mm, "end": v(18.95, 17.14) * mm});
            skLineSegment(sketch, "E16.31.26.0", {"start": v(18.92, 19.4) * mm, "end": v(19.17, 19.17) * mm});
            skLineSegment(sketch, "E16.34.26.0", {"start": v(19.4, 18.92) * mm, "end": v(19.17, 19.17) * mm});
            skArc(sketch, "E16.37.26.0", {"start": v(18.92, 19.4) * mm, "mid": v(18.82, 19.45) * mm, "end": v(18.7, 19.46) * mm});
            skArc(sketch, "E16.41.26.0", {"start": v(19.46, 18.7) * mm, "mid": v(19.45, 18.82) * mm, "end": v(19.4, 18.92) * mm});
            skArc(sketch, "E16.45.26.0", {"start": v(17.14, 18.95) * mm, "mid": v(17, 18.87) * mm, "end": v(16.9, 18.76) * mm});
            skArc(sketch, "E16.49.26.0", {"start": v(17, 18.88) * mm, "mid": v(17, 18.88) * mm, "end": v(17, 18.87) * mm});
            skArc(sketch, "E16.53.26.0", {"start": v(17, 18.88) * mm, "mid": v(17, 18.88) * mm, "end": v(17, 18.87) * mm});
            skArc(sketch, "E16.1.27.0", {"start": v(14.97, 20.7) * mm, "mid": v(15.1, 21.52) * mm, "end": v(15.14, 22.34) * mm});
            skPoint(sketch, "E16.4.27.0", {"position": v(14.93, 20.55) * mm});
            skPoint(sketch, "E16.5.27.0", {"position": v(12.7, 22) * mm});
            skLineSegment(sketch, "E16.6.27.0", {"start": v(14.84, 20.43) * mm, "end": v(14.4, 19.81) * mm});
            skArc(sketch, "E16.9.27.0", {"start": v(12.83, 22.1) * mm, "mid": v(13.51, 22.55) * mm, "end": v(14.25, 22.92) * mm});
            skArc(sketch, "E16.13.27.0", {"start": v(11.18, 20.9) * mm, "mid": v(11.78, 20.84) * mm, "end": v(12.25, 21.21) * mm});
            skPoint(sketch, "E16.17.27.0", {"position": v(13.94, 19.18) * mm});
            skArc(sketch, "E16.18.27.0", {"start": v(14.4, 19.81) * mm, "mid": v(14.25, 19.24) * mm, "end": v(14.55, 18.72) * mm});
            skPoint(sketch, "E16.22.27.0", {"position": v(15.14, 22.46) * mm});
            skPoint(sketch, "E16.23.27.0", {"position": v(14.36, 22.97) * mm});
            skLineSegment(sketch, "E16.24.27.0", {"start": v(12.62, 21.87) * mm, "end": v(12.25, 21.21) * mm});
            skArc(sketch, "E16.27.27.0", {"start": v(14.84, 20.43) * mm, "mid": v(14.92, 20.56) * mm, "end": v(14.97, 20.7) * mm});
            skLineSegment(sketch, "E16.31.27.0", {"start": v(14.47, 22.9) * mm, "end": v(14.76, 22.74) * mm});
            skLineSegment(sketch, "E16.34.27.0", {"start": v(15.04, 22.54) * mm, "end": v(14.76, 22.74) * mm});
            skArc(sketch, "E16.37.27.0", {"start": v(14.47, 22.9) * mm, "mid": v(14.36, 22.94) * mm, "end": v(14.25, 22.92) * mm});
            skArc(sketch, "E16.41.27.0", {"start": v(15.14, 22.34) * mm, "mid": v(15.11, 22.45) * mm, "end": v(15.04, 22.54) * mm});
            skArc(sketch, "E16.45.27.0", {"start": v(12.83, 22.1) * mm, "mid": v(12.71, 22) * mm, "end": v(12.62, 21.87) * mm});
            skArc(sketch, "E16.49.27.0", {"start": v(12.7, 22) * mm, "mid": v(12.7, 22) * mm, "end": v(12.7, 22) * mm});
            skArc(sketch, "E16.53.27.0", {"start": v(12.7, 22) * mm, "mid": v(12.7, 22) * mm, "end": v(12.7, 22) * mm});
            skArc(sketch, "E16.1.28.0", {"start": v(10.34, 23.37) * mm, "mid": v(10.3, 24.19) * mm, "end": v(10.17, 25) * mm});
            skPoint(sketch, "E16.4.28.0", {"position": v(10.33, 23.2) * mm});
            skPoint(sketch, "E16.5.28.0", {"position": v(7.85, 24.16) * mm});
            skLineSegment(sketch, "E16.6.28.0", {"start": v(10.27, 23.06) * mm, "end": v(9.96, 22.37) * mm});
            skArc(sketch, "E16.9.28.0", {"start": v(7.95, 24.28) * mm, "mid": v(8.53, 24.87) * mm, "end": v(9.17, 25.38) * mm});
            skArc(sketch, "E16.13.28.0", {"start": v(6.6, 22.78) * mm, "mid": v(7.19, 22.84) * mm, "end": v(7.57, 23.3) * mm});
            skPoint(sketch, "E16.17.28.0", {"position": v(9.64, 21.66) * mm});
            skArc(sketch, "E16.18.28.0", {"start": v(9.96, 22.37) * mm, "mid": v(9.94, 21.78) * mm, "end": v(10.34, 21.34) * mm});
            skPoint(sketch, "E16.22.28.0", {"position": v(10.14, 25.12) * mm});
            skPoint(sketch, "E16.23.28.0", {"position": v(9.28, 25.45) * mm});
            skLineSegment(sketch, "E16.24.28.0", {"start": v(7.8, 24.01) * mm, "end": v(7.57, 23.3) * mm});
            skArc(sketch, "E16.27.28.0", {"start": v(10.27, 23.06) * mm, "mid": v(10.32, 23.21) * mm, "end": v(10.34, 23.37) * mm});
            skLineSegment(sketch, "E16.31.28.0", {"start": v(9.4, 25.41) * mm, "end": v(9.72, 25.3) * mm});
            skLineSegment(sketch, "E16.34.28.0", {"start": v(10.02, 25.17) * mm, "end": v(9.72, 25.3) * mm});
            skArc(sketch, "E16.37.28.0", {"start": v(9.4, 25.41) * mm, "mid": v(9.28, 25.42) * mm, "end": v(9.17, 25.38) * mm});
            skArc(sketch, "E16.41.28.0", {"start": v(10.17, 25) * mm, "mid": v(10.12, 25.1) * mm, "end": v(10.02, 25.17) * mm});
            skArc(sketch, "E16.45.28.0", {"start": v(7.95, 24.28) * mm, "mid": v(7.86, 24.15) * mm, "end": v(7.8, 24.01) * mm});
            skArc(sketch, "E16.49.28.0", {"start": v(7.85, 24.16) * mm, "mid": v(7.85, 24.16) * mm, "end": v(7.85, 24.15) * mm});
            skArc(sketch, "E16.53.28.0", {"start": v(7.85, 24.16) * mm, "mid": v(7.85, 24.16) * mm, "end": v(7.85, 24.15) * mm});
            skArc(sketch, "E16.1.29.0", {"start": v(5.25, 25) * mm, "mid": v(5.05, 25.8) * mm, "end": v(4.75, 26.57) * mm});
            skPoint(sketch, "E16.4.29.0", {"position": v(5.28, 24.84) * mm});
            skPoint(sketch, "E16.5.29.0", {"position": v(2.66, 25.26) * mm});
            skLineSegment(sketch, "E16.6.29.0", {"start": v(5.25, 24.7) * mm, "end": v(5.1, 23.96) * mm});
            skArc(sketch, "E16.9.29.0", {"start": v(2.73, 25.4) * mm, "mid": v(3.17, 26.1) * mm, "end": v(3.7, 26.73) * mm});
            skArc(sketch, "E16.13.29.0", {"start": v(1.71, 23.65) * mm, "mid": v(2.28, 23.83) * mm, "end": v(2.56, 24.36) * mm});
            skPoint(sketch, "E16.17.29.0", {"position": v(4.93, 23.2) * mm});
            skArc(sketch, "E16.18.29.0", {"start": v(5.1, 23.96) * mm, "mid": v(5.2, 23.37) * mm, "end": v(5.68, 23.02) * mm});
            skPoint(sketch, "E16.22.29.0", {"position": v(4.7, 26.68) * mm});
            skPoint(sketch, "E16.23.29.0", {"position": v(3.78, 26.82) * mm});
            skLineSegment(sketch, "E16.24.29.0", {"start": v(2.64, 25.1) * mm, "end": v(2.56, 24.36) * mm});
            skArc(sketch, "E16.27.29.0", {"start": v(5.25, 24.7) * mm, "mid": v(5.27, 24.85) * mm, "end": v(5.25, 25) * mm});
            skLineSegment(sketch, "E16.31.29.0", {"start": v(3.9, 26.81) * mm, "end": v(4.24, 26.78) * mm});
            skLineSegment(sketch, "E16.34.29.0", {"start": v(4.57, 26.7) * mm, "end": v(4.24, 26.78) * mm});
            skArc(sketch, "E16.37.29.0", {"start": v(3.9, 26.81) * mm, "mid": v(3.79, 26.8) * mm, "end": v(3.7, 26.73) * mm});
            skArc(sketch, "E16.41.29.0", {"start": v(4.75, 26.57) * mm, "mid": v(4.68, 26.66) * mm, "end": v(4.57, 26.7) * mm});
            skArc(sketch, "E16.45.29.0", {"start": v(2.73, 25.4) * mm, "mid": v(2.67, 25.26) * mm, "end": v(2.64, 25.1) * mm});
            skArc(sketch, "E16.49.29.0", {"start": v(2.66, 25.26) * mm, "mid": v(2.66, 25.26) * mm, "end": v(2.65, 25.26) * mm});
            skArc(sketch, "E16.53.29.0", {"start": v(2.66, 25.26) * mm, "mid": v(2.66, 25.26) * mm, "end": v(2.65, 25.26) * mm});
            skArc(sketch, "E17.trimOffspring", {"start": v(-16.43, 17.1) * mm, "mid": v(-17.04, 16.5) * mm, "end": v(-17.62, 15.87) * mm});
            skArc(sketch, "E18.trimOffspring", {"start": v(-12.51, 20.14) * mm, "mid": v(-13.23, 19.67) * mm, "end": v(-13.94, 19.18) * mm});
            skArc(sketch, "E19.trimOffspring", {"start": v(-8.05, 22.3) * mm, "mid": v(-8.85, 22) * mm, "end": v(-9.64, 21.66) * mm});
            skArc(sketch, "E20.trimOffspring", {"start": v(1.71, 23.65) * mm, "mid": v(1.24, 23.68) * mm, "end": v(0.77, 23.7) * mm});
            skArc(sketch, "E21.trimOffspring", {"start": v(6.6, 22.78) * mm, "mid": v(5.77, 23) * mm, "end": v(4.93, 23.2) * mm});
            skArc(sketch, "E22.trimOffspring", {"start": v(11.18, 20.9) * mm, "mid": v(10.42, 21.3) * mm, "end": v(9.64, 21.66) * mm});
            skArc(sketch, "E23.trimOffspring", {"start": v(15.29, 18.13) * mm, "mid": v(14.62, 18.67) * mm, "end": v(13.94, 19.18) * mm});
            skArc(sketch, "E24.trimOffspring", {"start": v(18.72, 14.55) * mm, "mid": v(18.18, 15.22) * mm, "end": v(17.62, 15.87) * mm});
            skArc(sketch, "E25.trimOffspring", {"start": v(21.34, 10.34) * mm, "mid": v(20.95, 11.1) * mm, "end": v(20.53, 11.86) * mm});
            skArc(sketch, "E26.trimOffspring", {"start": v(23.02, 5.68) * mm, "mid": v(22.8, 6.5) * mm, "end": v(22.55, 7.33) * mm});
            skArc(sketch, "E27.trimOffspring", {"start": v(23.7, 0.77) * mm, "mid": v(23.66, 1.62) * mm, "end": v(23.58, 2.48) * mm});
            skArc(sketch, "E28.trimOffspring", {"start": v(23.34, -4.18) * mm, "mid": v(23.48, -3.33) * mm, "end": v(23.58, -2.48) * mm});
            skArc(sketch, "E29.trimOffspring", {"start": v(21.96, -8.94) * mm, "mid": v(22.27, -8.14) * mm, "end": v(22.55, -7.33) * mm});
            skArc(sketch, "E30.trimOffspring", {"start": v(19.62, -13.3) * mm, "mid": v(20.1, -12.6) * mm, "end": v(20.53, -11.86) * mm});
            skArc(sketch, "E31.trimOffspring", {"start": v(16.43, -17.1) * mm, "mid": v(17.04, -16.5) * mm, "end": v(17.62, -15.87) * mm});
            skArc(sketch, "E32.trimOffspring", {"start": v(12.51, -20.14) * mm, "mid": v(13.23, -19.67) * mm, "end": v(13.94, -19.18) * mm});
            skArc(sketch, "E33.trimOffspring", {"start": v(8.05, -22.3) * mm, "mid": v(8.85, -22) * mm, "end": v(9.64, -21.66) * mm});
            skArc(sketch, "E34.trimOffspring", {"start": v(3.24, -23.49) * mm, "mid": v(4.09, -23.36) * mm, "end": v(4.93, -23.2) * mm});
            skArc(sketch, "E35.trimOffspring", {"start": v(-1.71, -23.65) * mm, "mid": v(-0.86, -23.7) * mm, "end": v(0, -23.71) * mm});
            skArc(sketch, "E36.trimOffspring", {"start": v(-6.6, -22.78) * mm, "mid": v(-5.77, -23) * mm, "end": v(-4.93, -23.2) * mm});
            skArc(sketch, "E37.trimOffspring", {"start": v(-11.18, -20.9) * mm, "mid": v(-10.42, -21.3) * mm, "end": v(-9.64, -21.66) * mm});
            skArc(sketch, "E38.trimOffspring", {"start": v(-15.29, -18.13) * mm, "mid": v(-14.62, -18.67) * mm, "end": v(-13.94, -19.18) * mm});
            skArc(sketch, "E39.trimOffspring", {"start": v(-18.72, -14.55) * mm, "mid": v(-18.18, -15.22) * mm, "end": v(-17.62, -15.87) * mm});
            skArc(sketch, "E40.trimOffspring", {"start": v(-21.34, -10.34) * mm, "mid": v(-20.95, -11.1) * mm, "end": v(-20.53, -11.86) * mm});
            skArc(sketch, "E41.trimOffspring", {"start": v(-23.02, -5.68) * mm, "mid": v(-22.8, -6.5) * mm, "end": v(-22.55, -7.33) * mm});
            skArc(sketch, "E42.trimOffspring", {"start": v(-23.7, -0.77) * mm, "mid": v(-23.66, -1.62) * mm, "end": v(-23.58, -2.48) * mm});
            skArc(sketch, "E43.trimOffspring", {"start": v(-23.34, 4.18) * mm, "mid": v(-23.48, 3.33) * mm, "end": v(-23.58, 2.48) * mm});
            skArc(sketch, "E44.trimOffspring", {"start": v(-21.96, 8.94) * mm, "mid": v(-22.27, 8.14) * mm, "end": v(-22.55, 7.33) * mm});
            skArc(sketch, "E45.trimOffspring", {"start": v(-19.62, 13.3) * mm, "mid": v(-20.1, 12.6) * mm, "end": v(-20.53, 11.86) * mm});
            skSolve(sketch);
        }
        {
            var Q0;
            Q0=makeQuery(id+"F0.imprint","IMPRINT",FACE,{"disambiguationData":[TD([[makeQuery(id+"F0.imprint","IMPRINT",EDGE,{"derivedFrom":sQuery(id+"F0.wireOp",EDGE,"E1.trimOffspring")}),1.0]])]});
            cPlane(context, id + "F1", {"entities" : qUnion([Q0]), "cplaneType" : CPlaneType.OFFSET, "offset" : 22 * mm, "width" : 152.4 * mm, "height" : 152.4 * mm});
        }
        {
            var Q0;
            Q0=qCreatedBy(id+"F1.planeOp",FACE);
            var sketch = newSketch(context, id + "F2", { "sketchPlane" : qUnion([Q0])});
            skArc(sketch, "E46", {"start": v(-4.49, 35.28) * mm, "mid": v(-5.56, 35.12) * mm, "end": v(-6.63, 34.94) * mm});
            skArc(sketch, "E47.trimOffspring", {"start": v(-0.06, 38.25) * mm, "mid": v(-0.63, 39.42) * mm, "end": v(-1.36, 40.5) * mm});
            skLineSegment(sketch, "E48", {"start": v(-1.57, 40.6) * mm, "end": v(-2.13, 40.58) * mm});
            skLineSegment(sketch, "E49", {"start": v(0, 37.95) * mm, "end": v(0, 36.35) * mm});
            skLineSegment(sketch, "E50.MirrorCS", {"start": v(-2.68, 40.55) * mm, "end": v(-2.13, 40.58) * mm});
            skArc(sketch, "E51.MirrorCS", {"start": v(-3.94, 38.04) * mm, "mid": v(-3.5, 39.27) * mm, "end": v(-2.89, 40.43) * mm});
            skLineSegment(sketch, "E52.MirrorCS", {"start": v(-3.97, 37.74) * mm, "end": v(-3.8, 36.15) * mm});
            skPoint(sketch, "E53.orphan", {"position": v(-3.45, 32.82) * mm});
            skPoint(sketch, "E54.orphan", {"position": v(0, 33) * mm});
            skPoint(sketch, "E55.visualSharp", {"position": v(-3.72, 35.37) * mm});
            skArc(sketch, "E55.filletArc", {"start": v(-3.97, 35.34) * mm, "mid": v(-3.8, 35.43) * mm, "end": v(-3.74, 35.62) * mm});
            skArc(sketch, "E56.filletArc", {"start": v(-4.49, 35.28) * mm, "mid": v(-3.97, 35.57) * mm, "end": v(-3.8, 36.15) * mm});
            skPoint(sketch, "E57.visualSharp", {"position": v(0, 35.56) * mm});
            skArc(sketch, "E57.filletArc", {"start": v(0, 36.35) * mm, "mid": v(0.23, 35.79) * mm, "end": v(0.78, 35.55) * mm});
            skPoint(sketch, "E58.visualSharp", {"position": v(0, 38.1) * mm});
            skArc(sketch, "E58.filletArc", {"start": v(0, 37.95) * mm, "mid": v(-0.01, 38.1) * mm, "end": v(-0.06, 38.25) * mm});
            skPoint(sketch, "E59.visualSharp", {"position": v(-3.98, 37.9) * mm});
            skArc(sketch, "E59.filletArc", {"start": v(-3.94, 38.04) * mm, "mid": v(-3.97, 37.9) * mm, "end": v(-3.97, 37.74) * mm});
            skPoint(sketch, "E60.visualSharp", {"position": v(-2.81, 40.54) * mm});
            skArc(sketch, "E60.filletArc", {"start": v(-2.68, 40.55) * mm, "mid": v(-2.8, 40.51) * mm, "end": v(-2.89, 40.43) * mm});
            skPoint(sketch, "E61.visualSharp", {"position": v(-1.44, 40.61) * mm});
            skArc(sketch, "E61.filletArc", {"start": v(-1.36, 40.5) * mm, "mid": v(-1.45, 40.58) * mm, "end": v(-1.57, 40.6) * mm});
            skArc(sketch, "E62.1.0", {"start": v(-7.56, 35.55) * mm, "mid": v(-7.22, 35.05) * mm, "end": v(-6.63, 34.94) * mm});
            skArc(sketch, "E62.1.1", {"start": v(-11.72, 33.57) * mm, "mid": v(-11.28, 33.97) * mm, "end": v(-11.23, 34.57) * mm});
            skPoint(sketch, "E62.1.2", {"position": v(-7.92, 37.27) * mm});
            skArc(sketch, "E62.1.3", {"start": v(-8, 37.4) * mm, "mid": v(-8.81, 38.43) * mm, "end": v(-9.75, 39.34) * mm});
            skPoint(sketch, "E62.1.4", {"position": v(-9.85, 39.43) * mm});
            skPoint(sketch, "E62.1.5", {"position": v(-11.18, 39.07) * mm});
            skArc(sketch, "E62.1.6", {"start": v(-11.76, 36.4) * mm, "mid": v(-11.58, 37.69) * mm, "end": v(-11.23, 38.95) * mm});
            skLineSegment(sketch, "E62.1.7", {"start": v(-11.73, 36.1) * mm, "end": v(-11.23, 34.57) * mm});
            skLineSegment(sketch, "E62.1.8", {"start": v(-7.9, 37.12) * mm, "end": v(-7.56, 35.55) * mm});
            skPoint(sketch, "E62.1.9", {"position": v(-11.77, 36.24) * mm});
            skArc(sketch, "E62.1.10", {"start": v(-11.05, 39.1) * mm, "mid": v(-11.16, 39.05) * mm, "end": v(-11.23, 38.95) * mm});
            skArc(sketch, "E62.1.11", {"start": v(-11.76, 36.4) * mm, "mid": v(-11.76, 36.24) * mm, "end": v(-11.73, 36.1) * mm});
            skLineSegment(sketch, "E62.1.12", {"start": v(-9.98, 39.4) * mm, "end": v(-10.52, 39.25) * mm});
            skArc(sketch, "E62.1.13", {"start": v(-7.9, 37.12) * mm, "mid": v(-7.94, 37.27) * mm, "end": v(-8, 37.4) * mm});
            skArc(sketch, "E62.1.14", {"start": v(-9.75, 39.34) * mm, "mid": v(-9.86, 39.4) * mm, "end": v(-9.98, 39.4) * mm});
            skLineSegment(sketch, "E62.1.15", {"start": v(-11.05, 39.1) * mm, "end": v(-10.52, 39.25) * mm});
            skArc(sketch, "E62.2.0", {"start": v(-14.78, 33.2) * mm, "mid": v(-14.35, 32.79) * mm, "end": v(-13.75, 32.8) * mm});
            skArc(sketch, "E62.2.1", {"start": v(-18.45, 30.4) * mm, "mid": v(-18.1, 30.88) * mm, "end": v(-18.17, 31.48) * mm});
            skPoint(sketch, "E62.2.2", {"position": v(-15.5, 34.8) * mm});
            skArc(sketch, "E62.2.3", {"start": v(-15.6, 34.92) * mm, "mid": v(-16.6, 35.76) * mm, "end": v(-17.72, 36.46) * mm});
            skPoint(sketch, "E62.2.4", {"position": v(-17.83, 36.52) * mm});
            skPoint(sketch, "E62.2.5", {"position": v(-19.06, 35.9) * mm});
            skArc(sketch, "E62.2.6", {"start": v(-19.07, 33.15) * mm, "mid": v(-19.17, 34.46) * mm, "end": v(-19.08, 35.76) * mm});
            skLineSegment(sketch, "E62.2.7", {"start": v(-18.97, 32.87) * mm, "end": v(-18.17, 31.48) * mm});
            skLineSegment(sketch, "E62.2.8", {"start": v(-15.44, 34.67) * mm, "end": v(-14.78, 33.2) * mm});
            skPoint(sketch, "E62.2.9", {"position": v(-19.05, 33) * mm});
            skArc(sketch, "E62.2.10", {"start": v(-18.94, 35.95) * mm, "mid": v(-19.04, 35.87) * mm, "end": v(-19.08, 35.76) * mm});
            skArc(sketch, "E62.2.11", {"start": v(-19.07, 33.15) * mm, "mid": v(-19.04, 33) * mm, "end": v(-18.97, 32.87) * mm});
            skLineSegment(sketch, "E62.2.12", {"start": v(-17.95, 36.46) * mm, "end": v(-18.45, 36.2) * mm});
            skArc(sketch, "E62.2.13", {"start": v(-15.44, 34.67) * mm, "mid": v(-15.51, 34.8) * mm, "end": v(-15.6, 34.92) * mm});
            skArc(sketch, "E62.2.14", {"start": v(-17.72, 36.46) * mm, "mid": v(-17.83, 36.49) * mm, "end": v(-17.95, 36.46) * mm});
            skLineSegment(sketch, "E62.2.15", {"start": v(-18.94, 35.95) * mm, "end": v(-18.45, 36.2) * mm});
            skArc(sketch, "E63.3.3.0", {"start": v(-21.36, 29.4) * mm, "mid": v(-20.85, 29.09) * mm, "end": v(-20.27, 29.22) * mm});
            skArc(sketch, "E63.4.3.0", {"start": v(-24.37, 25.9) * mm, "mid": v(-24.12, 26.45) * mm, "end": v(-24.32, 27) * mm});
            skPoint(sketch, "E63.8.3.0", {"position": v(-22.4, 30.82) * mm});
            skArc(sketch, "E63.9.3.0", {"start": v(-22.53, 30.9) * mm, "mid": v(-23.68, 31.52) * mm, "end": v(-24.9, 31.98) * mm});
            skPoint(sketch, "E63.13.3.0", {"position": v(-25.04, 32.01) * mm});
            skPoint(sketch, "E63.14.3.0", {"position": v(-26.1, 31.15) * mm});
            skArc(sketch, "E63.15.3.0", {"start": v(-25.55, 28.46) * mm, "mid": v(-25.91, 29.72) * mm, "end": v(-26.1, 31.01) * mm});
            skLineSegment(sketch, "E63.19.3.0", {"start": v(-25.4, 28.2) * mm, "end": v(-24.32, 27) * mm});
            skLineSegment(sketch, "E63.22.3.0", {"start": v(-22.3, 30.7) * mm, "end": v(-21.36, 29.4) * mm});
            skPoint(sketch, "E63.25.3.0", {"position": v(-25.5, 28.31) * mm});
            skArc(sketch, "E63.26.3.0", {"start": v(-26, 31.23) * mm, "mid": v(-26.08, 31.13) * mm, "end": v(-26.1, 31.01) * mm});
            skArc(sketch, "E63.30.3.0", {"start": v(-25.55, 28.46) * mm, "mid": v(-25.48, 28.32) * mm, "end": v(-25.4, 28.2) * mm});
            skLineSegment(sketch, "E63.34.3.0", {"start": v(-25.14, 31.93) * mm, "end": v(-25.57, 31.58) * mm});
            skArc(sketch, "E63.37.3.0", {"start": v(-22.3, 30.7) * mm, "mid": v(-22.4, 30.82) * mm, "end": v(-22.53, 30.9) * mm});
            skArc(sketch, "E63.41.3.0", {"start": v(-24.9, 31.98) * mm, "mid": v(-25.03, 31.98) * mm, "end": v(-25.14, 31.93) * mm});
            skLineSegment(sketch, "E63.45.3.0", {"start": v(-26, 31.23) * mm, "end": v(-25.57, 31.58) * mm});
            skArc(sketch, "E63.3.4.0", {"start": v(-27, 24.32) * mm, "mid": v(-26.45, 24.12) * mm, "end": v(-25.9, 24.37) * mm});
            skArc(sketch, "E63.4.4.0", {"start": v(-29.22, 20.27) * mm, "mid": v(-29.09, 20.85) * mm, "end": v(-29.4, 21.36) * mm});
            skPoint(sketch, "E63.8.4.0", {"position": v(-28.31, 25.5) * mm});
            skArc(sketch, "E63.9.4.0", {"start": v(-28.46, 25.55) * mm, "mid": v(-29.72, 25.91) * mm, "end": v(-31.01, 26.1) * mm});
            skPoint(sketch, "E63.13.4.0", {"position": v(-31.15, 26.1) * mm});
            skPoint(sketch, "E63.14.4.0", {"position": v(-32.01, 25.04) * mm});
            skArc(sketch, "E63.15.4.0", {"start": v(-30.9, 22.53) * mm, "mid": v(-31.52, 23.68) * mm, "end": v(-31.98, 24.9) * mm});
            skLineSegment(sketch, "E63.19.4.0", {"start": v(-30.7, 22.3) * mm, "end": v(-29.4, 21.36) * mm});
            skLineSegment(sketch, "E63.22.4.0", {"start": v(-28.2, 25.4) * mm, "end": v(-27, 24.32) * mm});
            skPoint(sketch, "E63.25.4.0", {"position": v(-30.82, 22.4) * mm});
            skArc(sketch, "E63.26.4.0", {"start": v(-31.93, 25.14) * mm, "mid": v(-31.98, 25.03) * mm, "end": v(-31.98, 24.9) * mm});
            skArc(sketch, "E63.30.4.0", {"start": v(-30.9, 22.53) * mm, "mid": v(-30.82, 22.4) * mm, "end": v(-30.7, 22.3) * mm});
            skLineSegment(sketch, "E63.34.4.0", {"start": v(-31.23, 26) * mm, "end": v(-31.58, 25.57) * mm});
            skArc(sketch, "E63.37.4.0", {"start": v(-28.2, 25.4) * mm, "mid": v(-28.32, 25.48) * mm, "end": v(-28.46, 25.55) * mm});
            skArc(sketch, "E63.41.4.0", {"start": v(-31.01, 26.1) * mm, "mid": v(-31.13, 26.08) * mm, "end": v(-31.23, 26) * mm});
            skLineSegment(sketch, "E63.45.4.0", {"start": v(-31.93, 25.14) * mm, "end": v(-31.58, 25.57) * mm});
            skArc(sketch, "E63.3.5.0", {"start": v(-31.48, 18.17) * mm, "mid": v(-30.88, 18.1) * mm, "end": v(-30.4, 18.45) * mm});
            skArc(sketch, "E63.4.5.0", {"start": v(-32.8, 13.75) * mm, "mid": v(-32.79, 14.35) * mm, "end": v(-33.2, 14.78) * mm});
            skPoint(sketch, "E63.8.5.0", {"position": v(-33, 19.05) * mm});
            skArc(sketch, "E63.9.5.0", {"start": v(-33.15, 19.07) * mm, "mid": v(-34.46, 19.17) * mm, "end": v(-35.76, 19.08) * mm});
            skPoint(sketch, "E63.13.5.0", {"position": v(-35.9, 19.06) * mm});
            skPoint(sketch, "E63.14.5.0", {"position": v(-36.52, 17.83) * mm});
            skArc(sketch, "E63.15.5.0", {"start": v(-34.92, 15.6) * mm, "mid": v(-35.76, 16.6) * mm, "end": v(-36.46, 17.72) * mm});
            skLineSegment(sketch, "E63.19.5.0", {"start": v(-34.67, 15.44) * mm, "end": v(-33.2, 14.78) * mm});
            skLineSegment(sketch, "E63.22.5.0", {"start": v(-32.87, 18.97) * mm, "end": v(-31.48, 18.17) * mm});
            skPoint(sketch, "E63.25.5.0", {"position": v(-34.8, 15.5) * mm});
            skArc(sketch, "E63.26.5.0", {"start": v(-36.46, 17.95) * mm, "mid": v(-36.49, 17.83) * mm, "end": v(-36.46, 17.72) * mm});
            skArc(sketch, "E63.30.5.0", {"start": v(-34.92, 15.6) * mm, "mid": v(-34.8, 15.51) * mm, "end": v(-34.67, 15.44) * mm});
            skLineSegment(sketch, "E63.34.5.0", {"start": v(-35.95, 18.94) * mm, "end": v(-36.2, 18.45) * mm});
            skArc(sketch, "E63.37.5.0", {"start": v(-32.87, 18.97) * mm, "mid": v(-33, 19.04) * mm, "end": v(-33.15, 19.07) * mm});
            skArc(sketch, "E63.41.5.0", {"start": v(-35.76, 19.08) * mm, "mid": v(-35.87, 19.04) * mm, "end": v(-35.95, 18.94) * mm});
            skLineSegment(sketch, "E63.45.5.0", {"start": v(-36.46, 17.95) * mm, "end": v(-36.2, 18.45) * mm});
            skArc(sketch, "E63.3.6.0", {"start": v(-34.57, 11.23) * mm, "mid": v(-33.97, 11.28) * mm, "end": v(-33.57, 11.72) * mm});
            skArc(sketch, "E63.4.6.0", {"start": v(-34.94, 6.63) * mm, "mid": v(-35.05, 7.22) * mm, "end": v(-35.55, 7.56) * mm});
            skPoint(sketch, "E63.8.6.0", {"position": v(-36.24, 11.77) * mm});
            skArc(sketch, "E63.9.6.0", {"start": v(-36.4, 11.76) * mm, "mid": v(-37.69, 11.58) * mm, "end": v(-38.95, 11.23) * mm});
            skPoint(sketch, "E63.13.6.0", {"position": v(-39.07, 11.18) * mm});
            skPoint(sketch, "E63.14.6.0", {"position": v(-39.43, 9.85) * mm});
            skArc(sketch, "E63.15.6.0", {"start": v(-37.4, 8) * mm, "mid": v(-38.43, 8.81) * mm, "end": v(-39.34, 9.75) * mm});
            skLineSegment(sketch, "E63.19.6.0", {"start": v(-37.12, 7.9) * mm, "end": v(-35.55, 7.56) * mm});
            skLineSegment(sketch, "E63.22.6.0", {"start": v(-36.1, 11.73) * mm, "end": v(-34.57, 11.23) * mm});
            skPoint(sketch, "E63.25.6.0", {"position": v(-37.27, 7.92) * mm});
            skArc(sketch, "E63.26.6.0", {"start": v(-39.4, 9.98) * mm, "mid": v(-39.4, 9.86) * mm, "end": v(-39.34, 9.75) * mm});
            skArc(sketch, "E63.30.6.0", {"start": v(-37.4, 8) * mm, "mid": v(-37.27, 7.94) * mm, "end": v(-37.12, 7.9) * mm});
            skLineSegment(sketch, "E63.34.6.0", {"start": v(-39.1, 11.05) * mm, "end": v(-39.25, 10.52) * mm});
            skArc(sketch, "E63.37.6.0", {"start": v(-36.1, 11.73) * mm, "mid": v(-36.24, 11.76) * mm, "end": v(-36.4, 11.76) * mm});
            skArc(sketch, "E63.41.6.0", {"start": v(-38.95, 11.23) * mm, "mid": v(-39.05, 11.16) * mm, "end": v(-39.1, 11.05) * mm});
            skLineSegment(sketch, "E63.45.6.0", {"start": v(-39.4, 9.98) * mm, "end": v(-39.25, 10.52) * mm});
            skArc(sketch, "E63.3.7.0", {"start": v(-36.15, 3.8) * mm, "mid": v(-35.57, 3.97) * mm, "end": v(-35.28, 4.49) * mm});
            skArc(sketch, "E63.4.7.0", {"start": v(-35.55, -0.78) * mm, "mid": v(-35.79, -0.23) * mm, "end": v(-36.35, 0) * mm});
            skPoint(sketch, "E63.8.7.0", {"position": v(-37.9, 3.98) * mm});
            skArc(sketch, "E63.9.7.0", {"start": v(-38.04, 3.94) * mm, "mid": v(-39.27, 3.5) * mm, "end": v(-40.43, 2.89) * mm});
            skPoint(sketch, "E63.13.7.0", {"position": v(-40.54, 2.81) * mm});
            skPoint(sketch, "E63.14.7.0", {"position": v(-40.61, 1.44) * mm});
            skArc(sketch, "E63.15.7.0", {"start": v(-38.25, 0.06) * mm, "mid": v(-39.42, 0.63) * mm, "end": v(-40.5, 1.36) * mm});
            skLineSegment(sketch, "E63.19.7.0", {"start": v(-37.95, 0) * mm, "end": v(-36.35, 0) * mm});
            skLineSegment(sketch, "E63.22.7.0", {"start": v(-37.74, 3.97) * mm, "end": v(-36.15, 3.8) * mm});
            skPoint(sketch, "E63.25.7.0", {"position": v(-38.1, 0) * mm});
            skArc(sketch, "E63.26.7.0", {"start": v(-40.6, 1.57) * mm, "mid": v(-40.58, 1.45) * mm, "end": v(-40.5, 1.36) * mm});
            skArc(sketch, "E63.30.7.0", {"start": v(-38.25, 0.06) * mm, "mid": v(-38.1, 0.01) * mm, "end": v(-37.95, 0) * mm});
            skLineSegment(sketch, "E63.34.7.0", {"start": v(-40.55, 2.68) * mm, "end": v(-40.58, 2.13) * mm});
            skArc(sketch, "E63.37.7.0", {"start": v(-37.74, 3.97) * mm, "mid": v(-37.9, 3.97) * mm, "end": v(-38.04, 3.94) * mm});
            skArc(sketch, "E63.41.7.0", {"start": v(-40.43, 2.89) * mm, "mid": v(-40.51, 2.8) * mm, "end": v(-40.55, 2.68) * mm});
            skLineSegment(sketch, "E63.45.7.0", {"start": v(-40.6, 1.57) * mm, "end": v(-40.58, 2.13) * mm});
            skArc(sketch, "E63.3.8.0", {"start": v(-36.15, -3.8) * mm, "mid": v(-35.62, -3.52) * mm, "end": v(-35.44, -2.94) * mm});
            skArc(sketch, "E63.4.8.0", {"start": v(-34.61, -8.15) * mm, "mid": v(-34.96, -7.66) * mm, "end": v(-35.55, -7.56) * mm});
            skPoint(sketch, "E63.8.8.0", {"position": v(-37.9, -3.98) * mm});
            skArc(sketch, "E63.9.8.0", {"start": v(-38.03, -4.06) * mm, "mid": v(-39.14, -4.75) * mm, "end": v(-40.15, -5.58) * mm});
            skPoint(sketch, "E63.13.8.0", {"position": v(-40.24, -5.68) * mm});
            skPoint(sketch, "E63.14.8.0", {"position": v(-40.03, -7.04) * mm});
            skArc(sketch, "E63.15.8.0", {"start": v(-37.42, -7.9) * mm, "mid": v(-38.7, -7.58) * mm, "end": v(-39.9, -7.1) * mm});
            skLineSegment(sketch, "E63.19.8.0", {"start": v(-37.12, -7.9) * mm, "end": v(-35.55, -7.56) * mm});
            skLineSegment(sketch, "E63.22.8.0", {"start": v(-37.74, -3.97) * mm, "end": v(-36.15, -3.8) * mm});
            skPoint(sketch, "E63.25.8.0", {"position": v(-37.27, -7.92) * mm});
            skArc(sketch, "E63.26.8.0", {"start": v(-40.05, -6.9) * mm, "mid": v(-40, -7.02) * mm, "end": v(-39.9, -7.1) * mm});
            skArc(sketch, "E63.30.8.0", {"start": v(-37.42, -7.9) * mm, "mid": v(-37.27, -7.9) * mm, "end": v(-37.12, -7.9) * mm});
            skLineSegment(sketch, "E63.34.8.0", {"start": v(-40.22, -5.8) * mm, "end": v(-40.13, -6.36) * mm});
            skArc(sketch, "E63.37.8.0", {"start": v(-37.74, -3.97) * mm, "mid": v(-37.9, -4) * mm, "end": v(-38.03, -4.06) * mm});
            skArc(sketch, "E63.41.8.0", {"start": v(-40.15, -5.58) * mm, "mid": v(-40.21, -5.69) * mm, "end": v(-40.22, -5.8) * mm});
            skLineSegment(sketch, "E63.45.8.0", {"start": v(-40.05, -6.9) * mm, "end": v(-40.13, -6.36) * mm});
            skArc(sketch, "E63.3.9.0", {"start": v(-34.57, -11.23) * mm, "mid": v(-34.1, -10.84) * mm, "end": v(-34.05, -10.25) * mm});
            skArc(sketch, "E63.4.9.0", {"start": v(-32.16, -15.17) * mm, "mid": v(-32.6, -14.76) * mm, "end": v(-33.2, -14.78) * mm});
            skPoint(sketch, "E63.8.9.0", {"position": v(-36.24, -11.77) * mm});
            skArc(sketch, "E63.9.9.0", {"start": v(-36.36, -11.87) * mm, "mid": v(-37.3, -12.78) * mm, "end": v(-38.1, -13.8) * mm});
            skPoint(sketch, "E63.13.9.0", {"position": v(-38.18, -13.92) * mm});
            skPoint(sketch, "E63.14.9.0", {"position": v(-37.69, -15.2) * mm});
            skArc(sketch, "E63.15.9.0", {"start": v(-34.96, -15.5) * mm, "mid": v(-36.27, -15.46) * mm, "end": v(-37.56, -15.24) * mm});
            skLineSegment(sketch, "E63.19.9.0", {"start": v(-34.67, -15.44) * mm, "end": v(-33.2, -14.78) * mm});
            skLineSegment(sketch, "E63.22.9.0", {"start": v(-36.1, -11.73) * mm, "end": v(-34.57, -11.23) * mm});
            skPoint(sketch, "E63.25.9.0", {"position": v(-34.8, -15.5) * mm});
            skArc(sketch, "E63.26.9.0", {"start": v(-37.74, -15.08) * mm, "mid": v(-37.67, -15.18) * mm, "end": v(-37.56, -15.24) * mm});
            skArc(sketch, "E63.30.9.0", {"start": v(-34.96, -15.5) * mm, "mid": v(-34.81, -15.48) * mm, "end": v(-34.67, -15.44) * mm});
            skLineSegment(sketch, "E63.34.9.0", {"start": v(-38.13, -14.04) * mm, "end": v(-37.94, -14.56) * mm});
            skArc(sketch, "E63.37.9.0", {"start": v(-36.1, -11.73) * mm, "mid": v(-36.23, -11.79) * mm, "end": v(-36.36, -11.87) * mm});
            skArc(sketch, "E63.41.9.0", {"start": v(-38.1, -13.8) * mm, "mid": v(-38.15, -13.92) * mm, "end": v(-38.13, -14.04) * mm});
            skLineSegment(sketch, "E63.45.9.0", {"start": v(-37.74, -15.08) * mm, "end": v(-37.94, -14.56) * mm});
            skArc(sketch, "E63.3.10.0", {"start": v(-31.48, -18.17) * mm, "mid": v(-31.1, -17.7) * mm, "end": v(-31.18, -17.1) * mm});
            skArc(sketch, "E63.4.10.0", {"start": v(-28.3, -21.52) * mm, "mid": v(-28.82, -21.22) * mm, "end": v(-29.4, -21.36) * mm});
            skPoint(sketch, "E63.8.10.0", {"position": v(-33, -19.05) * mm});
            skArc(sketch, "E63.9.10.0", {"start": v(-33.1, -19.17) * mm, "mid": v(-33.83, -20.26) * mm, "end": v(-34.4, -21.43) * mm});
            skPoint(sketch, "E63.13.10.0", {"position": v(-34.45, -21.55) * mm});
            skPoint(sketch, "E63.14.10.0", {"position": v(-33.7, -22.7) * mm});
            skArc(sketch, "E63.15.10.0", {"start": v(-30.98, -22.43) * mm, "mid": v(-32.26, -22.66) * mm, "end": v(-33.57, -22.71) * mm});
            skLineSegment(sketch, "E63.19.10.0", {"start": v(-30.7, -22.3) * mm, "end": v(-29.4, -21.36) * mm});
            skLineSegment(sketch, "E63.22.10.0", {"start": v(-32.87, -18.97) * mm, "end": v(-31.48, -18.17) * mm});
            skPoint(sketch, "E63.25.10.0", {"position": v(-30.82, -22.4) * mm});
            skArc(sketch, "E63.26.10.0", {"start": v(-33.78, -22.6) * mm, "mid": v(-33.69, -22.68) * mm, "end": v(-33.57, -22.71) * mm});
            skArc(sketch, "E63.30.10.0", {"start": v(-30.98, -22.43) * mm, "mid": v(-30.83, -22.38) * mm, "end": v(-30.7, -22.3) * mm});
            skLineSegment(sketch, "E63.34.10.0", {"start": v(-34.38, -21.66) * mm, "end": v(-34.08, -22.13) * mm});
            skArc(sketch, "E63.37.10.0", {"start": v(-32.87, -18.97) * mm, "mid": v(-32.99, -19.06) * mm, "end": v(-33.1, -19.17) * mm});
            skArc(sketch, "E63.41.10.0", {"start": v(-34.4, -21.43) * mm, "mid": v(-34.42, -21.55) * mm, "end": v(-34.38, -21.66) * mm});
            skLineSegment(sketch, "E63.45.10.0", {"start": v(-33.78, -22.6) * mm, "end": v(-34.08, -22.13) * mm});
            skArc(sketch, "E63.3.11.0", {"start": v(-27, -24.32) * mm, "mid": v(-26.75, -23.78) * mm, "end": v(-26.94, -23.21) * mm});
            skArc(sketch, "E63.4.11.0", {"start": v(-23.21, -26.94) * mm, "mid": v(-23.78, -26.75) * mm, "end": v(-24.32, -27) * mm});
            skPoint(sketch, "E63.8.11.0", {"position": v(-28.31, -25.5) * mm});
            skArc(sketch, "E63.9.11.0", {"start": v(-28.38, -25.63) * mm, "mid": v(-28.88, -26.85) * mm, "end": v(-29.2, -28.11) * mm});
            skPoint(sketch, "E63.13.11.0", {"position": v(-29.22, -28.25) * mm});
            skPoint(sketch, "E63.14.11.0", {"position": v(-28.25, -29.22) * mm});
            skArc(sketch, "E63.15.11.0", {"start": v(-25.63, -28.38) * mm, "mid": v(-26.85, -28.88) * mm, "end": v(-28.11, -29.2) * mm});
            skLineSegment(sketch, "E63.19.11.0", {"start": v(-25.4, -28.2) * mm, "end": v(-24.32, -27) * mm});
            skLineSegment(sketch, "E63.22.11.0", {"start": v(-28.2, -25.4) * mm, "end": v(-27, -24.32) * mm});
            skPoint(sketch, "E63.25.11.0", {"position": v(-25.5, -28.31) * mm});
            skArc(sketch, "E63.26.11.0", {"start": v(-28.34, -29.13) * mm, "mid": v(-28.24, -29.19) * mm, "end": v(-28.11, -29.2) * mm});
            skArc(sketch, "E63.30.11.0", {"start": v(-25.63, -28.38) * mm, "mid": v(-25.5, -28.3) * mm, "end": v(-25.4, -28.2) * mm});
            skLineSegment(sketch, "E63.34.11.0", {"start": v(-29.13, -28.34) * mm, "end": v(-28.73, -28.73) * mm});
            skArc(sketch, "E63.37.11.0", {"start": v(-28.2, -25.4) * mm, "mid": v(-28.3, -25.5) * mm, "end": v(-28.38, -25.63) * mm});
            skArc(sketch, "E63.41.11.0", {"start": v(-29.2, -28.11) * mm, "mid": v(-29.19, -28.24) * mm, "end": v(-29.13, -28.34) * mm});
            skLineSegment(sketch, "E63.45.11.0", {"start": v(-28.34, -29.13) * mm, "end": v(-28.73, -28.73) * mm});
            skArc(sketch, "E63.3.12.0", {"start": v(-21.36, -29.4) * mm, "mid": v(-21.22, -28.82) * mm, "end": v(-21.52, -28.3) * mm});
            skArc(sketch, "E63.4.12.0", {"start": v(-17.1, -31.18) * mm, "mid": v(-17.7, -31.1) * mm, "end": v(-18.17, -31.48) * mm});
            skPoint(sketch, "E63.8.12.0", {"position": v(-22.4, -30.82) * mm});
            skArc(sketch, "E63.9.12.0", {"start": v(-22.43, -30.98) * mm, "mid": v(-22.66, -32.26) * mm, "end": v(-22.71, -33.57) * mm});
            skPoint(sketch, "E63.13.12.0", {"position": v(-22.7, -33.7) * mm});
            skPoint(sketch, "E63.14.12.0", {"position": v(-21.55, -34.45) * mm});
            skArc(sketch, "E63.15.12.0", {"start": v(-19.17, -33.1) * mm, "mid": v(-20.26, -33.83) * mm, "end": v(-21.43, -34.4) * mm});
            skLineSegment(sketch, "E63.19.12.0", {"start": v(-18.97, -32.87) * mm, "end": v(-18.17, -31.48) * mm});
            skLineSegment(sketch, "E63.22.12.0", {"start": v(-22.3, -30.7) * mm, "end": v(-21.36, -29.4) * mm});
            skPoint(sketch, "E63.25.12.0", {"position": v(-19.05, -33) * mm});
            skArc(sketch, "E63.26.12.0", {"start": v(-21.66, -34.38) * mm, "mid": v(-21.55, -34.42) * mm, "end": v(-21.43, -34.4) * mm});
            skArc(sketch, "E63.30.12.0", {"start": v(-19.17, -33.1) * mm, "mid": v(-19.06, -32.99) * mm, "end": v(-18.97, -32.87) * mm});
            skLineSegment(sketch, "E63.34.12.0", {"start": v(-22.6, -33.78) * mm, "end": v(-22.13, -34.08) * mm});
            skArc(sketch, "E63.37.12.0", {"start": v(-22.3, -30.7) * mm, "mid": v(-22.38, -30.83) * mm, "end": v(-22.43, -30.98) * mm});
            skArc(sketch, "E63.41.12.0", {"start": v(-22.71, -33.57) * mm, "mid": v(-22.68, -33.69) * mm, "end": v(-22.6, -33.78) * mm});
            skLineSegment(sketch, "E63.45.12.0", {"start": v(-21.66, -34.38) * mm, "end": v(-22.13, -34.08) * mm});
            skArc(sketch, "E63.3.13.0", {"start": v(-14.78, -33.2) * mm, "mid": v(-14.76, -32.6) * mm, "end": v(-15.17, -32.16) * mm});
            skArc(sketch, "E63.4.13.0", {"start": v(-10.25, -34.05) * mm, "mid": v(-10.84, -34.1) * mm, "end": v(-11.23, -34.57) * mm});
            skPoint(sketch, "E63.8.13.0", {"position": v(-15.5, -34.8) * mm});
            skArc(sketch, "E63.9.13.0", {"start": v(-15.5, -34.96) * mm, "mid": v(-15.46, -36.27) * mm, "end": v(-15.24, -37.56) * mm});
            skPoint(sketch, "E63.13.13.0", {"position": v(-15.2, -37.69) * mm});
            skPoint(sketch, "E63.14.13.0", {"position": v(-13.92, -38.18) * mm});
            skArc(sketch, "E63.15.13.0", {"start": v(-11.87, -36.36) * mm, "mid": v(-12.78, -37.3) * mm, "end": v(-13.8, -38.1) * mm});
            skLineSegment(sketch, "E63.19.13.0", {"start": v(-11.73, -36.1) * mm, "end": v(-11.23, -34.57) * mm});
            skLineSegment(sketch, "E63.22.13.0", {"start": v(-15.44, -34.67) * mm, "end": v(-14.78, -33.2) * mm});
            skPoint(sketch, "E63.25.13.0", {"position": v(-11.77, -36.24) * mm});
            skArc(sketch, "E63.26.13.0", {"start": v(-14.04, -38.13) * mm, "mid": v(-13.92, -38.15) * mm, "end": v(-13.8, -38.1) * mm});
            skArc(sketch, "E63.30.13.0", {"start": v(-11.87, -36.36) * mm, "mid": v(-11.79, -36.23) * mm, "end": v(-11.73, -36.1) * mm});
            skLineSegment(sketch, "E63.34.13.0", {"start": v(-15.08, -37.74) * mm, "end": v(-14.56, -37.94) * mm});
            skArc(sketch, "E63.37.13.0", {"start": v(-15.44, -34.67) * mm, "mid": v(-15.48, -34.81) * mm, "end": v(-15.5, -34.96) * mm});
            skArc(sketch, "E63.41.13.0", {"start": v(-15.24, -37.56) * mm, "mid": v(-15.18, -37.67) * mm, "end": v(-15.08, -37.74) * mm});
            skLineSegment(sketch, "E63.45.13.0", {"start": v(-14.04, -38.13) * mm, "end": v(-14.56, -37.94) * mm});
            skArc(sketch, "E63.3.14.0", {"start": v(-7.56, -35.55) * mm, "mid": v(-7.66, -34.96) * mm, "end": v(-8.15, -34.61) * mm});
            skArc(sketch, "E63.4.14.0", {"start": v(-2.94, -35.44) * mm, "mid": v(-3.52, -35.62) * mm, "end": v(-3.8, -36.15) * mm});
            skPoint(sketch, "E63.8.14.0", {"position": v(-7.92, -37.27) * mm});
            skArc(sketch, "E63.9.14.0", {"start": v(-7.9, -37.42) * mm, "mid": v(-7.58, -38.7) * mm, "end": v(-7.1, -39.9) * mm});
            skPoint(sketch, "E63.13.14.0", {"position": v(-7.04, -40.03) * mm});
            skPoint(sketch, "E63.14.14.0", {"position": v(-5.68, -40.24) * mm});
            skArc(sketch, "E63.15.14.0", {"start": v(-4.06, -38.03) * mm, "mid": v(-4.75, -39.14) * mm, "end": v(-5.58, -40.15) * mm});
            skLineSegment(sketch, "E63.19.14.0", {"start": v(-3.97, -37.74) * mm, "end": v(-3.8, -36.15) * mm});
            skLineSegment(sketch, "E63.22.14.0", {"start": v(-7.9, -37.12) * mm, "end": v(-7.56, -35.55) * mm});
            skPoint(sketch, "E63.25.14.0", {"position": v(-3.98, -37.9) * mm});
            skArc(sketch, "E63.26.14.0", {"start": v(-5.8, -40.22) * mm, "mid": v(-5.69, -40.21) * mm, "end": v(-5.58, -40.15) * mm});
            skArc(sketch, "E63.30.14.0", {"start": v(-4.06, -38.03) * mm, "mid": v(-4, -37.9) * mm, "end": v(-3.97, -37.74) * mm});
            skLineSegment(sketch, "E63.34.14.0", {"start": v(-6.9, -40.05) * mm, "end": v(-6.36, -40.13) * mm});
            skArc(sketch, "E63.37.14.0", {"start": v(-7.9, -37.12) * mm, "mid": v(-7.9, -37.27) * mm, "end": v(-7.9, -37.42) * mm});
            skArc(sketch, "E63.41.14.0", {"start": v(-7.1, -39.9) * mm, "mid": v(-7.02, -40) * mm, "end": v(-6.9, -40.05) * mm});
            skLineSegment(sketch, "E63.45.14.0", {"start": v(-5.8, -40.22) * mm, "end": v(-6.36, -40.13) * mm});
            skArc(sketch, "E63.3.15.0", {"start": v(0, -36.35) * mm, "mid": v(-0.23, -35.79) * mm, "end": v(-0.78, -35.55) * mm});
            skArc(sketch, "E63.4.15.0", {"start": v(4.49, -35.28) * mm, "mid": v(3.97, -35.57) * mm, "end": v(3.8, -36.15) * mm});
            skPoint(sketch, "E63.8.15.0", {"position": v(0, -38.1) * mm});
            skArc(sketch, "E63.9.15.0", {"start": v(0.06, -38.25) * mm, "mid": v(0.63, -39.42) * mm, "end": v(1.36, -40.5) * mm});
            skPoint(sketch, "E63.13.15.0", {"position": v(1.44, -40.61) * mm});
            skPoint(sketch, "E63.14.15.0", {"position": v(2.81, -40.54) * mm});
            skArc(sketch, "E63.15.15.0", {"start": v(3.94, -38.04) * mm, "mid": v(3.5, -39.27) * mm, "end": v(2.89, -40.43) * mm});
            skLineSegment(sketch, "E63.19.15.0", {"start": v(3.97, -37.74) * mm, "end": v(3.8, -36.15) * mm});
            skLineSegment(sketch, "E63.22.15.0", {"start": v(0, -37.95) * mm, "end": v(0, -36.35) * mm});
            skPoint(sketch, "E63.25.15.0", {"position": v(3.98, -37.9) * mm});
            skArc(sketch, "E63.26.15.0", {"start": v(2.68, -40.55) * mm, "mid": v(2.8, -40.51) * mm, "end": v(2.89, -40.43) * mm});
            skArc(sketch, "E63.30.15.0", {"start": v(3.94, -38.04) * mm, "mid": v(3.97, -37.9) * mm, "end": v(3.97, -37.74) * mm});
            skLineSegment(sketch, "E63.34.15.0", {"start": v(1.57, -40.6) * mm, "end": v(2.13, -40.58) * mm});
            skArc(sketch, "E63.37.15.0", {"start": v(0, -37.95) * mm, "mid": v(0.01, -38.1) * mm, "end": v(0.06, -38.25) * mm});
            skArc(sketch, "E63.41.15.0", {"start": v(1.36, -40.5) * mm, "mid": v(1.45, -40.58) * mm, "end": v(1.57, -40.6) * mm});
            skLineSegment(sketch, "E63.45.15.0", {"start": v(2.68, -40.55) * mm, "end": v(2.13, -40.58) * mm});
            skArc(sketch, "E63.3.16.0", {"start": v(7.56, -35.55) * mm, "mid": v(7.22, -35.05) * mm, "end": v(6.63, -34.94) * mm});
            skArc(sketch, "E63.4.16.0", {"start": v(11.72, -33.57) * mm, "mid": v(11.28, -33.97) * mm, "end": v(11.23, -34.57) * mm});
            skPoint(sketch, "E63.8.16.0", {"position": v(7.92, -37.27) * mm});
            skArc(sketch, "E63.9.16.0", {"start": v(8, -37.4) * mm, "mid": v(8.81, -38.43) * mm, "end": v(9.75, -39.34) * mm});
            skPoint(sketch, "E63.13.16.0", {"position": v(9.85, -39.43) * mm});
            skPoint(sketch, "E63.14.16.0", {"position": v(11.18, -39.07) * mm});
            skArc(sketch, "E63.15.16.0", {"start": v(11.76, -36.4) * mm, "mid": v(11.58, -37.69) * mm, "end": v(11.23, -38.95) * mm});
            skLineSegment(sketch, "E63.19.16.0", {"start": v(11.73, -36.1) * mm, "end": v(11.23, -34.57) * mm});
            skLineSegment(sketch, "E63.22.16.0", {"start": v(7.9, -37.12) * mm, "end": v(7.56, -35.55) * mm});
            skPoint(sketch, "E63.25.16.0", {"position": v(11.77, -36.24) * mm});
            skArc(sketch, "E63.26.16.0", {"start": v(11.05, -39.1) * mm, "mid": v(11.16, -39.05) * mm, "end": v(11.23, -38.95) * mm});
            skArc(sketch, "E63.30.16.0", {"start": v(11.76, -36.4) * mm, "mid": v(11.76, -36.24) * mm, "end": v(11.73, -36.1) * mm});
            skLineSegment(sketch, "E63.34.16.0", {"start": v(9.98, -39.4) * mm, "end": v(10.52, -39.25) * mm});
            skArc(sketch, "E63.37.16.0", {"start": v(7.9, -37.12) * mm, "mid": v(7.94, -37.27) * mm, "end": v(8, -37.4) * mm});
            skArc(sketch, "E63.41.16.0", {"start": v(9.75, -39.34) * mm, "mid": v(9.86, -39.4) * mm, "end": v(9.98, -39.4) * mm});
            skLineSegment(sketch, "E63.45.16.0", {"start": v(11.05, -39.1) * mm, "end": v(10.52, -39.25) * mm});
            skArc(sketch, "E63.3.17.0", {"start": v(14.78, -33.2) * mm, "mid": v(14.35, -32.79) * mm, "end": v(13.75, -32.8) * mm});
            skArc(sketch, "E63.4.17.0", {"start": v(18.45, -30.4) * mm, "mid": v(18.1, -30.88) * mm, "end": v(18.17, -31.48) * mm});
            skPoint(sketch, "E63.8.17.0", {"position": v(15.5, -34.8) * mm});
            skArc(sketch, "E63.9.17.0", {"start": v(15.6, -34.92) * mm, "mid": v(16.6, -35.76) * mm, "end": v(17.72, -36.46) * mm});
            skPoint(sketch, "E63.13.17.0", {"position": v(17.83, -36.52) * mm});
            skPoint(sketch, "E63.14.17.0", {"position": v(19.06, -35.9) * mm});
            skArc(sketch, "E63.15.17.0", {"start": v(19.07, -33.15) * mm, "mid": v(19.17, -34.46) * mm, "end": v(19.08, -35.76) * mm});
            skLineSegment(sketch, "E63.19.17.0", {"start": v(18.97, -32.87) * mm, "end": v(18.17, -31.48) * mm});
            skLineSegment(sketch, "E63.22.17.0", {"start": v(15.44, -34.67) * mm, "end": v(14.78, -33.2) * mm});
            skPoint(sketch, "E63.25.17.0", {"position": v(19.05, -33) * mm});
            skArc(sketch, "E63.26.17.0", {"start": v(18.94, -35.95) * mm, "mid": v(19.04, -35.87) * mm, "end": v(19.08, -35.76) * mm});
            skArc(sketch, "E63.30.17.0", {"start": v(19.07, -33.15) * mm, "mid": v(19.04, -33) * mm, "end": v(18.97, -32.87) * mm});
            skLineSegment(sketch, "E63.34.17.0", {"start": v(17.95, -36.46) * mm, "end": v(18.45, -36.2) * mm});
            skArc(sketch, "E63.37.17.0", {"start": v(15.44, -34.67) * mm, "mid": v(15.51, -34.8) * mm, "end": v(15.6, -34.92) * mm});
            skArc(sketch, "E63.41.17.0", {"start": v(17.72, -36.46) * mm, "mid": v(17.83, -36.49) * mm, "end": v(17.95, -36.46) * mm});
            skLineSegment(sketch, "E63.45.17.0", {"start": v(18.94, -35.95) * mm, "end": v(18.45, -36.2) * mm});
            skArc(sketch, "E63.3.18.0", {"start": v(21.36, -29.4) * mm, "mid": v(20.85, -29.09) * mm, "end": v(20.27, -29.22) * mm});
            skArc(sketch, "E63.4.18.0", {"start": v(24.37, -25.9) * mm, "mid": v(24.12, -26.45) * mm, "end": v(24.32, -27) * mm});
            skPoint(sketch, "E63.8.18.0", {"position": v(22.4, -30.82) * mm});
            skArc(sketch, "E63.9.18.0", {"start": v(22.53, -30.9) * mm, "mid": v(23.68, -31.52) * mm, "end": v(24.9, -31.98) * mm});
            skPoint(sketch, "E63.13.18.0", {"position": v(25.04, -32.01) * mm});
            skPoint(sketch, "E63.14.18.0", {"position": v(26.1, -31.15) * mm});
            skArc(sketch, "E63.15.18.0", {"start": v(25.55, -28.46) * mm, "mid": v(25.91, -29.72) * mm, "end": v(26.1, -31.01) * mm});
            skLineSegment(sketch, "E63.19.18.0", {"start": v(25.4, -28.2) * mm, "end": v(24.32, -27) * mm});
            skLineSegment(sketch, "E63.22.18.0", {"start": v(22.3, -30.7) * mm, "end": v(21.36, -29.4) * mm});
            skPoint(sketch, "E63.25.18.0", {"position": v(25.5, -28.31) * mm});
            skArc(sketch, "E63.26.18.0", {"start": v(26, -31.23) * mm, "mid": v(26.08, -31.13) * mm, "end": v(26.1, -31.01) * mm});
            skArc(sketch, "E63.30.18.0", {"start": v(25.55, -28.46) * mm, "mid": v(25.48, -28.32) * mm, "end": v(25.4, -28.2) * mm});
            skLineSegment(sketch, "E63.34.18.0", {"start": v(25.14, -31.93) * mm, "end": v(25.57, -31.58) * mm});
            skArc(sketch, "E63.37.18.0", {"start": v(22.3, -30.7) * mm, "mid": v(22.4, -30.82) * mm, "end": v(22.53, -30.9) * mm});
            skArc(sketch, "E63.41.18.0", {"start": v(24.9, -31.98) * mm, "mid": v(25.03, -31.98) * mm, "end": v(25.14, -31.93) * mm});
            skLineSegment(sketch, "E63.45.18.0", {"start": v(26, -31.23) * mm, "end": v(25.57, -31.58) * mm});
            skArc(sketch, "E63.3.19.0", {"start": v(27, -24.32) * mm, "mid": v(26.45, -24.12) * mm, "end": v(25.9, -24.37) * mm});
            skArc(sketch, "E63.4.19.0", {"start": v(29.22, -20.27) * mm, "mid": v(29.09, -20.85) * mm, "end": v(29.4, -21.36) * mm});
            skPoint(sketch, "E63.8.19.0", {"position": v(28.31, -25.5) * mm});
            skArc(sketch, "E63.9.19.0", {"start": v(28.46, -25.55) * mm, "mid": v(29.72, -25.91) * mm, "end": v(31.01, -26.1) * mm});
            skPoint(sketch, "E63.13.19.0", {"position": v(31.15, -26.1) * mm});
            skPoint(sketch, "E63.14.19.0", {"position": v(32.01, -25.04) * mm});
            skArc(sketch, "E63.15.19.0", {"start": v(30.9, -22.53) * mm, "mid": v(31.52, -23.68) * mm, "end": v(31.98, -24.9) * mm});
            skLineSegment(sketch, "E63.19.19.0", {"start": v(30.7, -22.3) * mm, "end": v(29.4, -21.36) * mm});
            skLineSegment(sketch, "E63.22.19.0", {"start": v(28.2, -25.4) * mm, "end": v(27, -24.32) * mm});
            skPoint(sketch, "E63.25.19.0", {"position": v(30.82, -22.4) * mm});
            skArc(sketch, "E63.26.19.0", {"start": v(31.93, -25.14) * mm, "mid": v(31.98, -25.03) * mm, "end": v(31.98, -24.9) * mm});
            skArc(sketch, "E63.30.19.0", {"start": v(30.9, -22.53) * mm, "mid": v(30.82, -22.4) * mm, "end": v(30.7, -22.3) * mm});
            skLineSegment(sketch, "E63.34.19.0", {"start": v(31.23, -26) * mm, "end": v(31.58, -25.57) * mm});
            skArc(sketch, "E63.37.19.0", {"start": v(28.2, -25.4) * mm, "mid": v(28.32, -25.48) * mm, "end": v(28.46, -25.55) * mm});
            skArc(sketch, "E63.41.19.0", {"start": v(31.01, -26.1) * mm, "mid": v(31.13, -26.08) * mm, "end": v(31.23, -26) * mm});
            skLineSegment(sketch, "E63.45.19.0", {"start": v(31.93, -25.14) * mm, "end": v(31.58, -25.57) * mm});
            skArc(sketch, "E63.3.20.0", {"start": v(31.48, -18.17) * mm, "mid": v(30.88, -18.1) * mm, "end": v(30.4, -18.45) * mm});
            skArc(sketch, "E63.4.20.0", {"start": v(32.8, -13.75) * mm, "mid": v(32.79, -14.35) * mm, "end": v(33.2, -14.78) * mm});
            skPoint(sketch, "E63.8.20.0", {"position": v(33, -19.05) * mm});
            skArc(sketch, "E63.9.20.0", {"start": v(33.15, -19.07) * mm, "mid": v(34.46, -19.17) * mm, "end": v(35.76, -19.08) * mm});
            skPoint(sketch, "E63.13.20.0", {"position": v(35.9, -19.06) * mm});
            skPoint(sketch, "E63.14.20.0", {"position": v(36.52, -17.83) * mm});
            skArc(sketch, "E63.15.20.0", {"start": v(34.92, -15.6) * mm, "mid": v(35.76, -16.6) * mm, "end": v(36.46, -17.72) * mm});
            skLineSegment(sketch, "E63.19.20.0", {"start": v(34.67, -15.44) * mm, "end": v(33.2, -14.78) * mm});
            skLineSegment(sketch, "E63.22.20.0", {"start": v(32.87, -18.97) * mm, "end": v(31.48, -18.17) * mm});
            skPoint(sketch, "E63.25.20.0", {"position": v(34.8, -15.5) * mm});
            skArc(sketch, "E63.26.20.0", {"start": v(36.46, -17.95) * mm, "mid": v(36.49, -17.83) * mm, "end": v(36.46, -17.72) * mm});
            skArc(sketch, "E63.30.20.0", {"start": v(34.92, -15.6) * mm, "mid": v(34.8, -15.51) * mm, "end": v(34.67, -15.44) * mm});
            skLineSegment(sketch, "E63.34.20.0", {"start": v(35.95, -18.94) * mm, "end": v(36.2, -18.45) * mm});
            skArc(sketch, "E63.37.20.0", {"start": v(32.87, -18.97) * mm, "mid": v(33, -19.04) * mm, "end": v(33.15, -19.07) * mm});
            skArc(sketch, "E63.41.20.0", {"start": v(35.76, -19.08) * mm, "mid": v(35.87, -19.04) * mm, "end": v(35.95, -18.94) * mm});
            skLineSegment(sketch, "E63.45.20.0", {"start": v(36.46, -17.95) * mm, "end": v(36.2, -18.45) * mm});
            skArc(sketch, "E63.3.21.0", {"start": v(34.57, -11.23) * mm, "mid": v(33.97, -11.28) * mm, "end": v(33.57, -11.72) * mm});
            skArc(sketch, "E63.4.21.0", {"start": v(34.94, -6.63) * mm, "mid": v(35.05, -7.22) * mm, "end": v(35.55, -7.56) * mm});
            skPoint(sketch, "E63.8.21.0", {"position": v(36.24, -11.77) * mm});
            skArc(sketch, "E63.9.21.0", {"start": v(36.4, -11.76) * mm, "mid": v(37.69, -11.58) * mm, "end": v(38.95, -11.23) * mm});
            skPoint(sketch, "E63.13.21.0", {"position": v(39.07, -11.18) * mm});
            skPoint(sketch, "E63.14.21.0", {"position": v(39.43, -9.85) * mm});
            skArc(sketch, "E63.15.21.0", {"start": v(37.4, -8) * mm, "mid": v(38.43, -8.81) * mm, "end": v(39.34, -9.75) * mm});
            skLineSegment(sketch, "E63.19.21.0", {"start": v(37.12, -7.9) * mm, "end": v(35.55, -7.56) * mm});
            skLineSegment(sketch, "E63.22.21.0", {"start": v(36.1, -11.73) * mm, "end": v(34.57, -11.23) * mm});
            skPoint(sketch, "E63.25.21.0", {"position": v(37.27, -7.92) * mm});
            skArc(sketch, "E63.26.21.0", {"start": v(39.4, -9.98) * mm, "mid": v(39.4, -9.86) * mm, "end": v(39.34, -9.75) * mm});
            skArc(sketch, "E63.30.21.0", {"start": v(37.4, -8) * mm, "mid": v(37.27, -7.94) * mm, "end": v(37.12, -7.9) * mm});
            skLineSegment(sketch, "E63.34.21.0", {"start": v(39.1, -11.05) * mm, "end": v(39.25, -10.52) * mm});
            skArc(sketch, "E63.37.21.0", {"start": v(36.1, -11.73) * mm, "mid": v(36.24, -11.76) * mm, "end": v(36.4, -11.76) * mm});
            skArc(sketch, "E63.41.21.0", {"start": v(38.95, -11.23) * mm, "mid": v(39.05, -11.16) * mm, "end": v(39.1, -11.05) * mm});
            skLineSegment(sketch, "E63.45.21.0", {"start": v(39.4, -9.98) * mm, "end": v(39.25, -10.52) * mm});
            skArc(sketch, "E63.3.22.0", {"start": v(36.15, -3.8) * mm, "mid": v(35.57, -3.97) * mm, "end": v(35.28, -4.49) * mm});
            skArc(sketch, "E63.4.22.0", {"start": v(35.55, 0.78) * mm, "mid": v(35.79, 0.23) * mm, "end": v(36.35, 0) * mm});
            skPoint(sketch, "E63.8.22.0", {"position": v(37.9, -3.98) * mm});
            skArc(sketch, "E63.9.22.0", {"start": v(38.04, -3.94) * mm, "mid": v(39.27, -3.5) * mm, "end": v(40.43, -2.89) * mm});
            skPoint(sketch, "E63.13.22.0", {"position": v(40.54, -2.81) * mm});
            skPoint(sketch, "E63.14.22.0", {"position": v(40.61, -1.44) * mm});
            skArc(sketch, "E63.15.22.0", {"start": v(38.25, -0.06) * mm, "mid": v(39.42, -0.63) * mm, "end": v(40.5, -1.36) * mm});
            skLineSegment(sketch, "E63.19.22.0", {"start": v(37.95, 0) * mm, "end": v(36.35, 0) * mm});
            skLineSegment(sketch, "E63.22.22.0", {"start": v(37.74, -3.97) * mm, "end": v(36.15, -3.8) * mm});
            skPoint(sketch, "E63.25.22.0", {"position": v(38.1, 0) * mm});
            skArc(sketch, "E63.26.22.0", {"start": v(40.6, -1.57) * mm, "mid": v(40.58, -1.45) * mm, "end": v(40.5, -1.36) * mm});
            skArc(sketch, "E63.30.22.0", {"start": v(38.25, -0.06) * mm, "mid": v(38.1, -0.01) * mm, "end": v(37.95, 0) * mm});
            skLineSegment(sketch, "E63.34.22.0", {"start": v(40.55, -2.68) * mm, "end": v(40.58, -2.13) * mm});
            skArc(sketch, "E63.37.22.0", {"start": v(37.74, -3.97) * mm, "mid": v(37.9, -3.97) * mm, "end": v(38.04, -3.94) * mm});
            skArc(sketch, "E63.41.22.0", {"start": v(40.43, -2.89) * mm, "mid": v(40.51, -2.8) * mm, "end": v(40.55, -2.68) * mm});
            skLineSegment(sketch, "E63.45.22.0", {"start": v(40.6, -1.57) * mm, "end": v(40.58, -2.13) * mm});
            skArc(sketch, "E63.3.23.0", {"start": v(36.15, 3.8) * mm, "mid": v(35.62, 3.52) * mm, "end": v(35.44, 2.94) * mm});
            skArc(sketch, "E63.4.23.0", {"start": v(34.61, 8.15) * mm, "mid": v(34.96, 7.66) * mm, "end": v(35.55, 7.56) * mm});
            skPoint(sketch, "E63.8.23.0", {"position": v(37.9, 3.98) * mm});
            skArc(sketch, "E63.9.23.0", {"start": v(38.03, 4.06) * mm, "mid": v(39.14, 4.75) * mm, "end": v(40.15, 5.58) * mm});
            skPoint(sketch, "E63.13.23.0", {"position": v(40.24, 5.68) * mm});
            skPoint(sketch, "E63.14.23.0", {"position": v(40.03, 7.04) * mm});
            skArc(sketch, "E63.15.23.0", {"start": v(37.42, 7.9) * mm, "mid": v(38.7, 7.58) * mm, "end": v(39.9, 7.1) * mm});
            skLineSegment(sketch, "E63.19.23.0", {"start": v(37.12, 7.9) * mm, "end": v(35.55, 7.56) * mm});
            skLineSegment(sketch, "E63.22.23.0", {"start": v(37.74, 3.97) * mm, "end": v(36.15, 3.8) * mm});
            skPoint(sketch, "E63.25.23.0", {"position": v(37.27, 7.92) * mm});
            skArc(sketch, "E63.26.23.0", {"start": v(40.05, 6.9) * mm, "mid": v(40, 7.02) * mm, "end": v(39.9, 7.1) * mm});
            skArc(sketch, "E63.30.23.0", {"start": v(37.42, 7.9) * mm, "mid": v(37.27, 7.9) * mm, "end": v(37.12, 7.9) * mm});
            skLineSegment(sketch, "E63.34.23.0", {"start": v(40.22, 5.8) * mm, "end": v(40.13, 6.36) * mm});
            skArc(sketch, "E63.37.23.0", {"start": v(37.74, 3.97) * mm, "mid": v(37.9, 4) * mm, "end": v(38.03, 4.06) * mm});
            skArc(sketch, "E63.41.23.0", {"start": v(40.15, 5.58) * mm, "mid": v(40.21, 5.69) * mm, "end": v(40.22, 5.8) * mm});
            skLineSegment(sketch, "E63.45.23.0", {"start": v(40.05, 6.9) * mm, "end": v(40.13, 6.36) * mm});
            skArc(sketch, "E63.3.24.0", {"start": v(34.57, 11.23) * mm, "mid": v(34.1, 10.84) * mm, "end": v(34.05, 10.25) * mm});
            skArc(sketch, "E63.4.24.0", {"start": v(32.16, 15.17) * mm, "mid": v(32.6, 14.76) * mm, "end": v(33.2, 14.78) * mm});
            skPoint(sketch, "E63.8.24.0", {"position": v(36.24, 11.77) * mm});
            skArc(sketch, "E63.9.24.0", {"start": v(36.36, 11.87) * mm, "mid": v(37.3, 12.78) * mm, "end": v(38.1, 13.8) * mm});
            skPoint(sketch, "E63.13.24.0", {"position": v(38.18, 13.92) * mm});
            skPoint(sketch, "E63.14.24.0", {"position": v(37.69, 15.2) * mm});
            skArc(sketch, "E63.15.24.0", {"start": v(34.96, 15.5) * mm, "mid": v(36.27, 15.46) * mm, "end": v(37.56, 15.24) * mm});
            skLineSegment(sketch, "E63.19.24.0", {"start": v(34.67, 15.44) * mm, "end": v(33.2, 14.78) * mm});
            skLineSegment(sketch, "E63.22.24.0", {"start": v(36.1, 11.73) * mm, "end": v(34.57, 11.23) * mm});
            skPoint(sketch, "E63.25.24.0", {"position": v(34.8, 15.5) * mm});
            skArc(sketch, "E63.26.24.0", {"start": v(37.74, 15.08) * mm, "mid": v(37.67, 15.18) * mm, "end": v(37.56, 15.24) * mm});
            skArc(sketch, "E63.30.24.0", {"start": v(34.96, 15.5) * mm, "mid": v(34.81, 15.48) * mm, "end": v(34.67, 15.44) * mm});
            skLineSegment(sketch, "E63.34.24.0", {"start": v(38.13, 14.04) * mm, "end": v(37.94, 14.56) * mm});
            skArc(sketch, "E63.37.24.0", {"start": v(36.1, 11.73) * mm, "mid": v(36.23, 11.79) * mm, "end": v(36.36, 11.87) * mm});
            skArc(sketch, "E63.41.24.0", {"start": v(38.1, 13.8) * mm, "mid": v(38.15, 13.92) * mm, "end": v(38.13, 14.04) * mm});
            skLineSegment(sketch, "E63.45.24.0", {"start": v(37.74, 15.08) * mm, "end": v(37.94, 14.56) * mm});
            skArc(sketch, "E63.3.25.0", {"start": v(31.48, 18.17) * mm, "mid": v(31.1, 17.7) * mm, "end": v(31.18, 17.1) * mm});
            skArc(sketch, "E63.4.25.0", {"start": v(28.3, 21.52) * mm, "mid": v(28.82, 21.22) * mm, "end": v(29.4, 21.36) * mm});
            skPoint(sketch, "E63.8.25.0", {"position": v(33, 19.05) * mm});
            skArc(sketch, "E63.9.25.0", {"start": v(33.1, 19.17) * mm, "mid": v(33.83, 20.26) * mm, "end": v(34.4, 21.43) * mm});
            skPoint(sketch, "E63.13.25.0", {"position": v(34.45, 21.55) * mm});
            skPoint(sketch, "E63.14.25.0", {"position": v(33.7, 22.7) * mm});
            skArc(sketch, "E63.15.25.0", {"start": v(30.98, 22.43) * mm, "mid": v(32.26, 22.66) * mm, "end": v(33.57, 22.71) * mm});
            skLineSegment(sketch, "E63.19.25.0", {"start": v(30.7, 22.3) * mm, "end": v(29.4, 21.36) * mm});
            skLineSegment(sketch, "E63.22.25.0", {"start": v(32.87, 18.97) * mm, "end": v(31.48, 18.17) * mm});
            skPoint(sketch, "E63.25.25.0", {"position": v(30.82, 22.4) * mm});
            skArc(sketch, "E63.26.25.0", {"start": v(33.78, 22.6) * mm, "mid": v(33.69, 22.68) * mm, "end": v(33.57, 22.71) * mm});
            skArc(sketch, "E63.30.25.0", {"start": v(30.98, 22.43) * mm, "mid": v(30.83, 22.38) * mm, "end": v(30.7, 22.3) * mm});
            skLineSegment(sketch, "E63.34.25.0", {"start": v(34.38, 21.66) * mm, "end": v(34.08, 22.13) * mm});
            skArc(sketch, "E63.37.25.0", {"start": v(32.87, 18.97) * mm, "mid": v(32.99, 19.06) * mm, "end": v(33.1, 19.17) * mm});
            skArc(sketch, "E63.41.25.0", {"start": v(34.4, 21.43) * mm, "mid": v(34.42, 21.55) * mm, "end": v(34.38, 21.66) * mm});
            skLineSegment(sketch, "E63.45.25.0", {"start": v(33.78, 22.6) * mm, "end": v(34.08, 22.13) * mm});
            skArc(sketch, "E63.3.26.0", {"start": v(27, 24.32) * mm, "mid": v(26.75, 23.78) * mm, "end": v(26.94, 23.21) * mm});
            skArc(sketch, "E63.4.26.0", {"start": v(23.21, 26.94) * mm, "mid": v(23.78, 26.75) * mm, "end": v(24.32, 27) * mm});
            skPoint(sketch, "E63.8.26.0", {"position": v(28.31, 25.5) * mm});
            skArc(sketch, "E63.9.26.0", {"start": v(28.38, 25.63) * mm, "mid": v(28.88, 26.85) * mm, "end": v(29.2, 28.11) * mm});
            skPoint(sketch, "E63.13.26.0", {"position": v(29.22, 28.25) * mm});
            skPoint(sketch, "E63.14.26.0", {"position": v(28.25, 29.22) * mm});
            skArc(sketch, "E63.15.26.0", {"start": v(25.63, 28.38) * mm, "mid": v(26.85, 28.88) * mm, "end": v(28.11, 29.2) * mm});
            skLineSegment(sketch, "E63.19.26.0", {"start": v(25.4, 28.2) * mm, "end": v(24.32, 27) * mm});
            skLineSegment(sketch, "E63.22.26.0", {"start": v(28.2, 25.4) * mm, "end": v(27, 24.32) * mm});
            skPoint(sketch, "E63.25.26.0", {"position": v(25.5, 28.31) * mm});
            skArc(sketch, "E63.26.26.0", {"start": v(28.34, 29.13) * mm, "mid": v(28.24, 29.19) * mm, "end": v(28.11, 29.2) * mm});
            skArc(sketch, "E63.30.26.0", {"start": v(25.63, 28.38) * mm, "mid": v(25.5, 28.3) * mm, "end": v(25.4, 28.2) * mm});
            skLineSegment(sketch, "E63.34.26.0", {"start": v(29.13, 28.34) * mm, "end": v(28.73, 28.73) * mm});
            skArc(sketch, "E63.37.26.0", {"start": v(28.2, 25.4) * mm, "mid": v(28.3, 25.5) * mm, "end": v(28.38, 25.63) * mm});
            skArc(sketch, "E63.41.26.0", {"start": v(29.2, 28.11) * mm, "mid": v(29.19, 28.24) * mm, "end": v(29.13, 28.34) * mm});
            skLineSegment(sketch, "E63.45.26.0", {"start": v(28.34, 29.13) * mm, "end": v(28.73, 28.73) * mm});
            skArc(sketch, "E63.3.27.0", {"start": v(21.36, 29.4) * mm, "mid": v(21.22, 28.82) * mm, "end": v(21.52, 28.3) * mm});
            skArc(sketch, "E63.4.27.0", {"start": v(17.1, 31.18) * mm, "mid": v(17.7, 31.1) * mm, "end": v(18.17, 31.48) * mm});
            skPoint(sketch, "E63.8.27.0", {"position": v(22.4, 30.82) * mm});
            skArc(sketch, "E63.9.27.0", {"start": v(22.43, 30.98) * mm, "mid": v(22.66, 32.26) * mm, "end": v(22.71, 33.57) * mm});
            skPoint(sketch, "E63.13.27.0", {"position": v(22.7, 33.7) * mm});
            skPoint(sketch, "E63.14.27.0", {"position": v(21.55, 34.45) * mm});
            skArc(sketch, "E63.15.27.0", {"start": v(19.17, 33.1) * mm, "mid": v(20.26, 33.83) * mm, "end": v(21.43, 34.4) * mm});
            skLineSegment(sketch, "E63.19.27.0", {"start": v(18.97, 32.87) * mm, "end": v(18.17, 31.48) * mm});
            skLineSegment(sketch, "E63.22.27.0", {"start": v(22.3, 30.7) * mm, "end": v(21.36, 29.4) * mm});
            skPoint(sketch, "E63.25.27.0", {"position": v(19.05, 33) * mm});
            skArc(sketch, "E63.26.27.0", {"start": v(21.66, 34.38) * mm, "mid": v(21.55, 34.42) * mm, "end": v(21.43, 34.4) * mm});
            skArc(sketch, "E63.30.27.0", {"start": v(19.17, 33.1) * mm, "mid": v(19.06, 32.99) * mm, "end": v(18.97, 32.87) * mm});
            skLineSegment(sketch, "E63.34.27.0", {"start": v(22.6, 33.78) * mm, "end": v(22.13, 34.08) * mm});
            skArc(sketch, "E63.37.27.0", {"start": v(22.3, 30.7) * mm, "mid": v(22.38, 30.83) * mm, "end": v(22.43, 30.98) * mm});
            skArc(sketch, "E63.41.27.0", {"start": v(22.71, 33.57) * mm, "mid": v(22.68, 33.69) * mm, "end": v(22.6, 33.78) * mm});
            skLineSegment(sketch, "E63.45.27.0", {"start": v(21.66, 34.38) * mm, "end": v(22.13, 34.08) * mm});
            skArc(sketch, "E63.3.28.0", {"start": v(14.78, 33.2) * mm, "mid": v(14.76, 32.6) * mm, "end": v(15.17, 32.16) * mm});
            skArc(sketch, "E63.4.28.0", {"start": v(10.25, 34.05) * mm, "mid": v(10.84, 34.1) * mm, "end": v(11.23, 34.57) * mm});
            skPoint(sketch, "E63.8.28.0", {"position": v(15.5, 34.8) * mm});
            skArc(sketch, "E63.9.28.0", {"start": v(15.5, 34.96) * mm, "mid": v(15.46, 36.27) * mm, "end": v(15.24, 37.56) * mm});
            skPoint(sketch, "E63.13.28.0", {"position": v(15.2, 37.69) * mm});
            skPoint(sketch, "E63.14.28.0", {"position": v(13.92, 38.18) * mm});
            skArc(sketch, "E63.15.28.0", {"start": v(11.87, 36.36) * mm, "mid": v(12.78, 37.3) * mm, "end": v(13.8, 38.1) * mm});
            skLineSegment(sketch, "E63.19.28.0", {"start": v(11.73, 36.1) * mm, "end": v(11.23, 34.57) * mm});
            skLineSegment(sketch, "E63.22.28.0", {"start": v(15.44, 34.67) * mm, "end": v(14.78, 33.2) * mm});
            skPoint(sketch, "E63.25.28.0", {"position": v(11.77, 36.24) * mm});
            skArc(sketch, "E63.26.28.0", {"start": v(14.04, 38.13) * mm, "mid": v(13.92, 38.15) * mm, "end": v(13.8, 38.1) * mm});
            skArc(sketch, "E63.30.28.0", {"start": v(11.87, 36.36) * mm, "mid": v(11.79, 36.23) * mm, "end": v(11.73, 36.1) * mm});
            skLineSegment(sketch, "E63.34.28.0", {"start": v(15.08, 37.74) * mm, "end": v(14.56, 37.94) * mm});
            skArc(sketch, "E63.37.28.0", {"start": v(15.44, 34.67) * mm, "mid": v(15.48, 34.81) * mm, "end": v(15.5, 34.96) * mm});
            skArc(sketch, "E63.41.28.0", {"start": v(15.24, 37.56) * mm, "mid": v(15.18, 37.67) * mm, "end": v(15.08, 37.74) * mm});
            skLineSegment(sketch, "E63.45.28.0", {"start": v(14.04, 38.13) * mm, "end": v(14.56, 37.94) * mm});
            skArc(sketch, "E63.3.29.0", {"start": v(7.56, 35.55) * mm, "mid": v(7.66, 34.96) * mm, "end": v(8.15, 34.61) * mm});
            skArc(sketch, "E63.4.29.0", {"start": v(2.94, 35.44) * mm, "mid": v(3.52, 35.62) * mm, "end": v(3.8, 36.15) * mm});
            skPoint(sketch, "E63.8.29.0", {"position": v(7.92, 37.27) * mm});
            skArc(sketch, "E63.9.29.0", {"start": v(7.9, 37.42) * mm, "mid": v(7.58, 38.7) * mm, "end": v(7.1, 39.9) * mm});
            skPoint(sketch, "E63.13.29.0", {"position": v(7.04, 40.03) * mm});
            skPoint(sketch, "E63.14.29.0", {"position": v(5.68, 40.24) * mm});
            skArc(sketch, "E63.15.29.0", {"start": v(4.06, 38.03) * mm, "mid": v(4.75, 39.14) * mm, "end": v(5.58, 40.15) * mm});
            skLineSegment(sketch, "E63.19.29.0", {"start": v(3.97, 37.74) * mm, "end": v(3.8, 36.15) * mm});
            skLineSegment(sketch, "E63.22.29.0", {"start": v(7.9, 37.12) * mm, "end": v(7.56, 35.55) * mm});
            skPoint(sketch, "E63.25.29.0", {"position": v(3.98, 37.9) * mm});
            skArc(sketch, "E63.26.29.0", {"start": v(5.8, 40.22) * mm, "mid": v(5.69, 40.21) * mm, "end": v(5.58, 40.15) * mm});
            skArc(sketch, "E63.30.29.0", {"start": v(4.06, 38.03) * mm, "mid": v(4, 37.9) * mm, "end": v(3.97, 37.74) * mm});
            skLineSegment(sketch, "E63.34.29.0", {"start": v(6.9, 40.05) * mm, "end": v(6.36, 40.13) * mm});
            skArc(sketch, "E63.37.29.0", {"start": v(7.9, 37.12) * mm, "mid": v(7.9, 37.27) * mm, "end": v(7.9, 37.42) * mm});
            skArc(sketch, "E63.41.29.0", {"start": v(7.1, 39.9) * mm, "mid": v(7.02, 40) * mm, "end": v(6.9, 40.05) * mm});
            skLineSegment(sketch, "E63.45.29.0", {"start": v(5.8, 40.22) * mm, "end": v(6.36, 40.13) * mm});
            skArc(sketch, "E64.trimOffspring", {"start": v(2.94, 35.44) * mm, "mid": v(1.86, 35.51) * mm, "end": v(0.78, 35.55) * mm});
            skArc(sketch, "E65.trimOffspring", {"start": v(10.25, 34.05) * mm, "mid": v(9.2, 34.35) * mm, "end": v(8.15, 34.61) * mm});
            skArc(sketch, "E66.trimOffspring", {"start": v(17.1, 31.18) * mm, "mid": v(16.14, 31.68) * mm, "end": v(15.17, 32.16) * mm});
            skArc(sketch, "E67.trimOffspring", {"start": v(23.21, 26.94) * mm, "mid": v(22.38, 27.64) * mm, "end": v(21.52, 28.3) * mm});
            skArc(sketch, "E68.trimOffspring", {"start": v(28.3, 21.52) * mm, "mid": v(27.64, 22.38) * mm, "end": v(26.94, 23.21) * mm});
            skArc(sketch, "E69.trimOffspring", {"start": v(32.16, 15.17) * mm, "mid": v(31.68, 16.14) * mm, "end": v(31.18, 17.1) * mm});
            skArc(sketch, "E70.trimOffspring", {"start": v(34.61, 8.15) * mm, "mid": v(34.35, 9.2) * mm, "end": v(34.05, 10.25) * mm});
            skArc(sketch, "E71.trimOffspring", {"start": v(35.55, 0.78) * mm, "mid": v(35.51, 1.86) * mm, "end": v(35.44, 2.94) * mm});
            skArc(sketch, "E72.trimOffspring", {"start": v(34.94, -6.63) * mm, "mid": v(35.12, -5.56) * mm, "end": v(35.28, -4.49) * mm});
            skArc(sketch, "E73.trimOffspring", {"start": v(32.8, -13.75) * mm, "mid": v(33.2, -12.74) * mm, "end": v(33.57, -11.72) * mm});
            skArc(sketch, "E74.trimOffspring", {"start": v(29.22, -20.27) * mm, "mid": v(29.82, -19.37) * mm, "end": v(30.4, -18.45) * mm});
            skArc(sketch, "E75.trimOffspring", {"start": v(-11.72, 33.57) * mm, "mid": v(-12.74, 33.2) * mm, "end": v(-13.75, 32.8) * mm});
            skArc(sketch, "E76.trimOffspring", {"start": v(-18.45, 30.4) * mm, "mid": v(-19.37, 29.82) * mm, "end": v(-20.27, 29.22) * mm});
            skArc(sketch, "E77.trimOffspring", {"start": v(24.37, -25.9) * mm, "mid": v(25.14, -25.14) * mm, "end": v(25.9, -24.37) * mm});
            skArc(sketch, "E78.trimOffspring", {"start": v(18.45, -30.4) * mm, "mid": v(19.37, -29.82) * mm, "end": v(20.27, -29.22) * mm});
            skArc(sketch, "E79.trimOffspring", {"start": v(11.72, -33.57) * mm, "mid": v(12.74, -33.2) * mm, "end": v(13.75, -32.8) * mm});
            skArc(sketch, "E80.trimOffspring", {"start": v(4.49, -35.28) * mm, "mid": v(5.56, -35.12) * mm, "end": v(6.63, -34.94) * mm});
            skArc(sketch, "E81.trimOffspring", {"start": v(-2.94, -35.44) * mm, "mid": v(-1.86, -35.51) * mm, "end": v(-0.78, -35.55) * mm});
            skArc(sketch, "E82.trimOffspring", {"start": v(-10.25, -34.05) * mm, "mid": v(-9.2, -34.35) * mm, "end": v(-8.15, -34.61) * mm});
            skArc(sketch, "E83.trimOffspring", {"start": v(-17.1, -31.18) * mm, "mid": v(-16.14, -31.68) * mm, "end": v(-15.17, -32.16) * mm});
            skArc(sketch, "E84.trimOffspring", {"start": v(-23.21, -26.94) * mm, "mid": v(-22.38, -27.64) * mm, "end": v(-21.52, -28.3) * mm});
            skArc(sketch, "E85.trimOffspring", {"start": v(-28.3, -21.52) * mm, "mid": v(-27.64, -22.38) * mm, "end": v(-26.94, -23.21) * mm});
            skArc(sketch, "E86.trimOffspring", {"start": v(-32.16, -15.17) * mm, "mid": v(-31.68, -16.14) * mm, "end": v(-31.18, -17.1) * mm});
            skArc(sketch, "E87.trimOffspring", {"start": v(-34.61, -8.15) * mm, "mid": v(-34.35, -9.2) * mm, "end": v(-34.05, -10.25) * mm});
            skArc(sketch, "E88.trimOffspring", {"start": v(-35.55, -0.78) * mm, "mid": v(-35.51, -1.86) * mm, "end": v(-35.44, -2.94) * mm});
            skArc(sketch, "E89.trimOffspring", {"start": v(-34.94, 6.63) * mm, "mid": v(-35.12, 5.56) * mm, "end": v(-35.28, 4.49) * mm});
            skArc(sketch, "E90.trimOffspring", {"start": v(-32.8, 13.75) * mm, "mid": v(-33.2, 12.74) * mm, "end": v(-33.57, 11.72) * mm});
            skArc(sketch, "E91.trimOffspring", {"start": v(-29.22, 20.27) * mm, "mid": v(-29.82, 19.37) * mm, "end": v(-30.4, 18.45) * mm});
            skArc(sketch, "E92.trimOffspring", {"start": v(-24.37, 25.9) * mm, "mid": v(-25.14, 25.14) * mm, "end": v(-25.9, 24.37) * mm});
            skSolve(sketch);
        }
        {
            var Q0;
            Q0=makeQuery(id+"F2.imprint","IMPRINT",FACE,{"disambiguationData":[TD([[makeQuery(id+"F2.imprint","IMPRINT",EDGE,{"derivedFrom":sQuery(id+"F2.wireOp",EDGE,"E46")}),1.0]])]});
            var Q1;
            Q1=makeQuery(id+"F0.imprint","IMPRINT",FACE,{"disambiguationData":[TD([[makeQuery(id+"F0.imprint","IMPRINT",EDGE,{"derivedFrom":sQuery(id+"F0.wireOp",EDGE,"E1.trimOffspring")}),1.0]])]});
            var Q2;
            Q2=sQuery(id+"F2.wireOp",VERTEX,"E62.1.15.end");
            var Q3;
            Q3=sQuery(id+"F0.wireOp",VERTEX,"E16.34.29.0.end");
            loft(context, id + "F3", {"sheetProfilesArray" : [{ "sheetProfileEntities" : qUnion([Q0]) }, { "sheetProfileEntities" : qUnion([Q1]) }], "matchConnections" : true, "connections" : [{ "connectionEntities" : qUnion([Q2, Q3]), "connectionEdgeQueries" : qUnion([]), "connectionEdgeParameters" : [] }]});
        }
        {
            var Q0;
            Q0=sQuery(id+"F2.wireOp",VERTEX,"E46.center");
            var Q1;
            Q1=makeQuery(id+"F3.opLoft","SWEPT_BODY",BODY,{"disambiguationData":[OSD([makeQuery(id+"F0.imprint","IMPRINT",FACE,{"disambiguationData":[TD([[makeQuery(id+"F0.imprint","IMPRINT",EDGE,{"derivedFrom":sQuery(id+"F0.wireOp",EDGE,"E1.trimOffspring")}),1.0]])]}),makeQuery(id+"F2.imprint","IMPRINT",FACE,{"disambiguationData":[TD([[makeQuery(id+"F2.imprint","IMPRINT",EDGE,{"derivedFrom":sQuery(id+"F2.wireOp",EDGE,"E46")}),1.0]])]})])]});
            hole(context, id + "F4", {"style" : HoleStyle.SIMPLE, "endStyle" : HoleEndStyle.THROUGH, "holeDiameter" : 12.7 * mm, "tappedDepth" : 12.7 * mm, "tapClearance" : 3, "locations" : qUnion([Q0]), "scope" : qUnion([Q1])});
        }
    });
